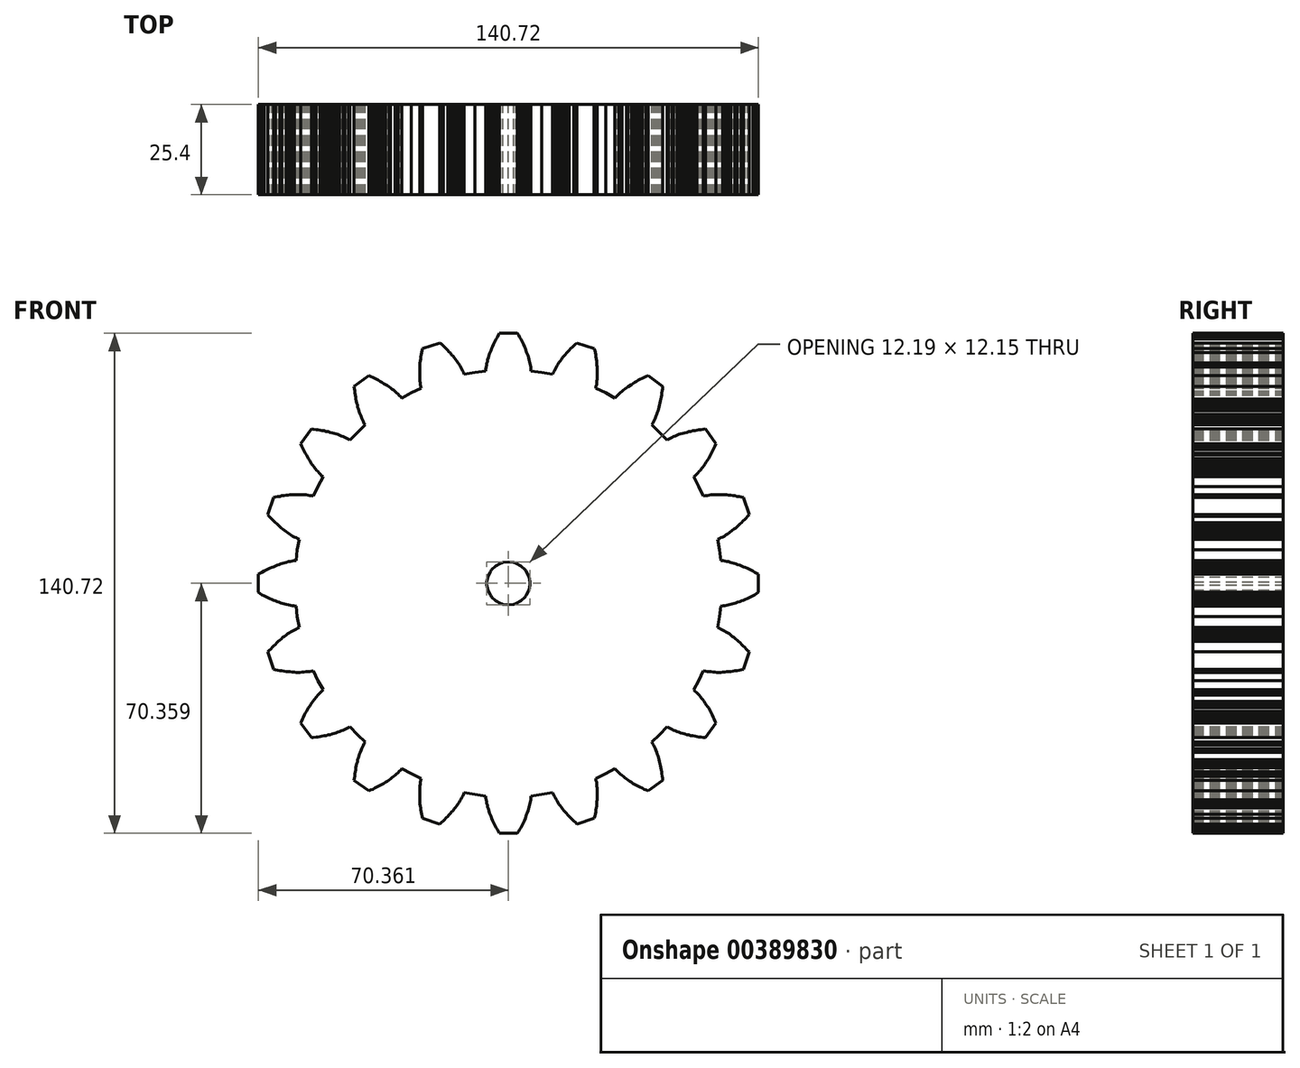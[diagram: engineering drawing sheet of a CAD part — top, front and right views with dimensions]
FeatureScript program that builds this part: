
annotation { "Feature Type Name" : "Feature", "Feature Type Description" : "" }
export const myFeature = defineFeature(function(context is Context, id is Id, definition is map)
    precondition{}
    {
        {
            var Q0;
            Q0=qCreatedBy(makeId("Front.planeOp"),FACE);
            var sketch = newSketch(context, id + "F0", { "sketchPlane" : qUnion([Q0])});
            skLineSegment(sketch, "E0", {"start": v(-98.04, 127.68) * mm, "end": v(-97.87, 127.68) * mm});
            skLineSegment(sketch, "E1", {"start": v(5.93, 25.9) * mm, "end": v(5.93, 25.45) * mm});
            skLineSegment(sketch, "E2", {"start": v(5.93, 25.45) * mm, "end": v(5.62, 24.07) * mm});
            skLineSegment(sketch, "E3", {"start": v(5.62, 24.07) * mm, "end": v(4.93, 22.63) * mm});
            skLineSegment(sketch, "E4", {"start": v(4.93, 22.63) * mm, "end": v(4.74, 22.35) * mm});
            skLineSegment(sketch, "E5", {"start": v(4.74, 22.35) * mm, "end": v(4.55, 22.08) * mm});
            skLineSegment(sketch, "E6", {"start": v(4.55, 22.08) * mm, "end": v(3.4, 21) * mm});
            skLineSegment(sketch, "E7", {"start": v(3.4, 21) * mm, "end": v(2, 20.26) * mm});
            skLineSegment(sketch, "E8", {"start": v(2, 20.26) * mm, "end": v(1.7, 20.15) * mm});
            skLineSegment(sketch, "E9", {"start": v(1.7, 20.15) * mm, "end": v(1.37, 20.05) * mm});
            skLineSegment(sketch, "E10", {"start": v(1.37, 20.05) * mm, "end": v(-0.17, 19.83) * mm});
            skLineSegment(sketch, "E11", {"start": v(-0.17, 19.83) * mm, "end": v(-1.72, 20.05) * mm});
            skLineSegment(sketch, "E12", {"start": v(-1.72, 20.05) * mm, "end": v(-2.03, 20.15) * mm});
            skLineSegment(sketch, "E13", {"start": v(-2.03, 20.15) * mm, "end": v(-2.35, 20.26) * mm});
            skLineSegment(sketch, "E14", {"start": v(-2.35, 20.26) * mm, "end": v(-3.75, 21) * mm});
            skLineSegment(sketch, "E15", {"start": v(-3.75, 21) * mm, "end": v(-4.9, 22.08) * mm});
            skLineSegment(sketch, "E16", {"start": v(-4.9, 22.08) * mm, "end": v(-5.08, 22.35) * mm});
            skLineSegment(sketch, "E17", {"start": v(-5.08, 22.35) * mm, "end": v(-5.27, 22.63) * mm});
            skLineSegment(sketch, "E18", {"start": v(-5.27, 22.63) * mm, "end": v(-5.96, 24.07) * mm});
            skLineSegment(sketch, "E19", {"start": v(-5.96, 24.07) * mm, "end": v(-6.27, 25.45) * mm});
            skLineSegment(sketch, "E20", {"start": v(-6.27, 25.45) * mm, "end": v(-6.27, 25.9) * mm});
            skLineSegment(sketch, "E21", {"start": v(-6.27, 25.9) * mm, "end": v(-6.27, 26.37) * mm});
            skLineSegment(sketch, "E22", {"start": v(-6.27, 26.37) * mm, "end": v(-5.96, 27.75) * mm});
            skLineSegment(sketch, "E23", {"start": v(-5.96, 27.75) * mm, "end": v(-5.27, 29.2) * mm});
            skLineSegment(sketch, "E24", {"start": v(-5.27, 29.2) * mm, "end": v(-5.08, 29.46) * mm});
            skLineSegment(sketch, "E25", {"start": v(-5.08, 29.46) * mm, "end": v(-4.9, 29.74) * mm});
            skLineSegment(sketch, "E26", {"start": v(-4.9, 29.74) * mm, "end": v(-3.75, 30.82) * mm});
            skLineSegment(sketch, "E27", {"start": v(-3.75, 30.82) * mm, "end": v(-2.35, 31.56) * mm});
            skLineSegment(sketch, "E28", {"start": v(-2.35, 31.56) * mm, "end": v(-2.03, 31.67) * mm});
            skLineSegment(sketch, "E29", {"start": v(-2.03, 31.67) * mm, "end": v(-1.72, 31.77) * mm});
            skLineSegment(sketch, "E30", {"start": v(-1.72, 31.77) * mm, "end": v(-0.17, 31.98) * mm});
            skLineSegment(sketch, "E31", {"start": v(-0.17, 31.98) * mm, "end": v(1.37, 31.77) * mm});
            skLineSegment(sketch, "E32", {"start": v(1.37, 31.77) * mm, "end": v(1.7, 31.67) * mm});
            skLineSegment(sketch, "E33", {"start": v(1.7, 31.67) * mm, "end": v(2, 31.56) * mm});
            skLineSegment(sketch, "E34", {"start": v(2, 31.56) * mm, "end": v(3.4, 30.82) * mm});
            skLineSegment(sketch, "E35", {"start": v(3.4, 30.82) * mm, "end": v(4.55, 29.74) * mm});
            skLineSegment(sketch, "E36", {"start": v(4.55, 29.74) * mm, "end": v(4.74, 29.46) * mm});
            skLineSegment(sketch, "E37", {"start": v(4.74, 29.46) * mm, "end": v(4.93, 29.2) * mm});
            skLineSegment(sketch, "E38", {"start": v(4.93, 29.2) * mm, "end": v(5.62, 27.75) * mm});
            skLineSegment(sketch, "E39", {"start": v(5.62, 27.75) * mm, "end": v(5.93, 26.37) * mm});
            skLineSegment(sketch, "E40", {"start": v(5.93, 26.37) * mm, "end": v(5.93, 25.9) * mm});
            skLineSegment(sketch, "E41", {"start": v(59.27, 16.5) * mm, "end": v(59.6, 19.47) * mm});
            skLineSegment(sketch, "E42", {"start": v(59.6, 19.47) * mm, "end": v(60.2, 19.56) * mm});
            skLineSegment(sketch, "E43", {"start": v(60.2, 19.56) * mm, "end": v(60.7, 19.64) * mm});
            skLineSegment(sketch, "E44", {"start": v(60.7, 19.64) * mm, "end": v(61.21, 19.73) * mm});
            skLineSegment(sketch, "E45", {"start": v(61.21, 19.73) * mm, "end": v(61.72, 19.81) * mm});
            skLineSegment(sketch, "E46", {"start": v(61.72, 19.81) * mm, "end": v(62.23, 19.98) * mm});
            skLineSegment(sketch, "E47", {"start": v(62.23, 19.98) * mm, "end": v(62.82, 20.07) * mm});
            skLineSegment(sketch, "E48", {"start": v(62.82, 20.07) * mm, "end": v(63.33, 20.24) * mm});
            skLineSegment(sketch, "E49", {"start": v(63.33, 20.24) * mm, "end": v(63.84, 20.4) * mm});
            skLineSegment(sketch, "E50", {"start": v(63.84, 20.4) * mm, "end": v(64.35, 20.57) * mm});
            skLineSegment(sketch, "E51", {"start": v(64.35, 20.57) * mm, "end": v(64.94, 20.74) * mm});
            skLineSegment(sketch, "E52", {"start": v(64.94, 20.74) * mm, "end": v(65.45, 21) * mm});
            skLineSegment(sketch, "E53", {"start": v(65.45, 21) * mm, "end": v(65.95, 21.17) * mm});
            skLineSegment(sketch, "E54", {"start": v(65.95, 21.17) * mm, "end": v(66.46, 21.42) * mm});
            skLineSegment(sketch, "E55", {"start": v(66.46, 21.42) * mm, "end": v(67.06, 21.67) * mm});
            skLineSegment(sketch, "E56", {"start": v(67.06, 21.67) * mm, "end": v(67.56, 21.93) * mm});
            skLineSegment(sketch, "E57", {"start": v(67.56, 21.93) * mm, "end": v(68.07, 22.18) * mm});
            skLineSegment(sketch, "E58", {"start": v(68.07, 22.18) * mm, "end": v(68.58, 22.44) * mm});
            skLineSegment(sketch, "E59", {"start": v(68.58, 22.44) * mm, "end": v(69.17, 22.7) * mm});
            skLineSegment(sketch, "E60", {"start": v(69.17, 22.7) * mm, "end": v(69.68, 23.03) * mm});
            skLineSegment(sketch, "E61", {"start": v(69.68, 23.03) * mm, "end": v(70.19, 23.37) * mm});
            skLineSegment(sketch, "E62", {"start": v(70.19, 23.37) * mm, "end": v(70.19, 28.45) * mm});
            skLineSegment(sketch, "E63", {"start": v(70.19, 28.45) * mm, "end": v(69.68, 28.79) * mm});
            skLineSegment(sketch, "E64", {"start": v(69.68, 28.79) * mm, "end": v(69.17, 29.04) * mm});
            skLineSegment(sketch, "E65", {"start": v(69.17, 29.04) * mm, "end": v(68.58, 29.38) * mm});
            skLineSegment(sketch, "E66", {"start": v(68.58, 29.38) * mm, "end": v(68.07, 29.63) * mm});
            skLineSegment(sketch, "E67", {"start": v(68.07, 29.63) * mm, "end": v(67.56, 29.89) * mm});
            skLineSegment(sketch, "E68", {"start": v(67.56, 29.89) * mm, "end": v(67.06, 30.14) * mm});
            skLineSegment(sketch, "E69", {"start": v(67.06, 30.14) * mm, "end": v(66.46, 30.4) * mm});
            skLineSegment(sketch, "E70", {"start": v(66.46, 30.4) * mm, "end": v(65.95, 30.56) * mm});
            skLineSegment(sketch, "E71", {"start": v(65.95, 30.56) * mm, "end": v(65.45, 30.82) * mm});
            skLineSegment(sketch, "E72", {"start": v(65.45, 30.82) * mm, "end": v(64.94, 30.99) * mm});
            skLineSegment(sketch, "E73", {"start": v(64.94, 30.99) * mm, "end": v(64.35, 31.16) * mm});
            skLineSegment(sketch, "E74", {"start": v(64.35, 31.16) * mm, "end": v(63.84, 31.41) * mm});
            skLineSegment(sketch, "E75", {"start": v(63.84, 31.41) * mm, "end": v(63.33, 31.58) * mm});
            skLineSegment(sketch, "E76", {"start": v(63.33, 31.58) * mm, "end": v(62.82, 31.67) * mm});
            skLineSegment(sketch, "E77", {"start": v(62.82, 31.67) * mm, "end": v(62.23, 31.83) * mm});
            skLineSegment(sketch, "E78", {"start": v(62.23, 31.83) * mm, "end": v(61.72, 32) * mm});
            skLineSegment(sketch, "E79", {"start": v(61.72, 32) * mm, "end": v(61.21, 32.09) * mm});
            skLineSegment(sketch, "E80", {"start": v(61.21, 32.09) * mm, "end": v(60.7, 32.17) * mm});
            skLineSegment(sketch, "E81", {"start": v(60.7, 32.17) * mm, "end": v(60.2, 32.26) * mm});
            skLineSegment(sketch, "E82", {"start": v(60.2, 32.26) * mm, "end": v(59.6, 32.26) * mm});
            skLineSegment(sketch, "E83", {"start": v(59.6, 32.26) * mm, "end": v(59.27, 35.3) * mm});
            skLineSegment(sketch, "E84", {"start": v(59.27, 35.3) * mm, "end": v(58.67, 38.27) * mm});
            skLineSegment(sketch, "E85", {"start": v(58.67, 38.27) * mm, "end": v(59.18, 38.52) * mm});
            skLineSegment(sketch, "E86", {"start": v(59.18, 38.52) * mm, "end": v(59.6, 38.78) * mm});
            skLineSegment(sketch, "E87", {"start": v(59.6, 38.78) * mm, "end": v(60.11, 38.95) * mm});
            skLineSegment(sketch, "E88", {"start": v(60.11, 38.95) * mm, "end": v(60.62, 39.2) * mm});
            skLineSegment(sketch, "E89", {"start": v(60.62, 39.2) * mm, "end": v(61.05, 39.54) * mm});
            skLineSegment(sketch, "E90", {"start": v(61.05, 39.54) * mm, "end": v(61.47, 39.8) * mm});
            skLineSegment(sketch, "E91", {"start": v(61.47, 39.8) * mm, "end": v(61.98, 40.13) * mm});
            skLineSegment(sketch, "E92", {"start": v(61.98, 40.13) * mm, "end": v(62.4, 40.47) * mm});
            skLineSegment(sketch, "E93", {"start": v(62.4, 40.47) * mm, "end": v(62.82, 40.81) * mm});
            skLineSegment(sketch, "E94", {"start": v(62.82, 40.81) * mm, "end": v(63.33, 41.15) * mm});
            skLineSegment(sketch, "E95", {"start": v(63.33, 41.15) * mm, "end": v(63.75, 41.49) * mm});
            skLineSegment(sketch, "E96", {"start": v(63.75, 41.49) * mm, "end": v(64.18, 41.83) * mm});
            skLineSegment(sketch, "E97", {"start": v(64.18, 41.83) * mm, "end": v(64.6, 42.25) * mm});
            skLineSegment(sketch, "E98", {"start": v(64.6, 42.25) * mm, "end": v(65.02, 42.67) * mm});
            skLineSegment(sketch, "E99", {"start": v(65.02, 42.67) * mm, "end": v(65.45, 43.01) * mm});
            skLineSegment(sketch, "E100", {"start": v(65.45, 43.01) * mm, "end": v(65.87, 43.43) * mm});
            skLineSegment(sketch, "E101", {"start": v(65.87, 43.43) * mm, "end": v(66.3, 43.86) * mm});
            skLineSegment(sketch, "E102", {"start": v(66.3, 43.86) * mm, "end": v(66.72, 44.28) * mm});
            skLineSegment(sketch, "E103", {"start": v(66.72, 44.28) * mm, "end": v(67.14, 44.7) * mm});
            skLineSegment(sketch, "E104", {"start": v(67.14, 44.7) * mm, "end": v(67.56, 45.21) * mm});
            skLineSegment(sketch, "E105", {"start": v(67.56, 45.21) * mm, "end": v(65.95, 50.04) * mm});
            skLineSegment(sketch, "E106", {"start": v(65.95, 50.04) * mm, "end": v(65.36, 50.2) * mm});
            skLineSegment(sketch, "E107", {"start": v(65.36, 50.2) * mm, "end": v(64.77, 50.3) * mm});
            skLineSegment(sketch, "E108", {"start": v(64.77, 50.3) * mm, "end": v(64.18, 50.38) * mm});
            skLineSegment(sketch, "E109", {"start": v(64.18, 50.38) * mm, "end": v(63.58, 50.55) * mm});
            skLineSegment(sketch, "E110", {"start": v(63.58, 50.55) * mm, "end": v(63, 50.63) * mm});
            skLineSegment(sketch, "E111", {"start": v(63, 50.63) * mm, "end": v(62.4, 50.72) * mm});
            skLineSegment(sketch, "E112", {"start": v(62.4, 50.72) * mm, "end": v(61.8, 50.72) * mm});
            skLineSegment(sketch, "E113", {"start": v(61.8, 50.72) * mm, "end": v(61.3, 50.8) * mm});
            skLineSegment(sketch, "E114", {"start": v(61.3, 50.8) * mm, "end": v(60.7, 50.8) * mm});
            skLineSegment(sketch, "E115", {"start": v(60.7, 50.8) * mm, "end": v(60.11, 50.88) * mm});
            skLineSegment(sketch, "E116", {"start": v(60.11, 50.88) * mm, "end": v(59.6, 50.88) * mm});
            skLineSegment(sketch, "E117", {"start": v(59.6, 50.88) * mm, "end": v(59.01, 50.88) * mm});
            skLineSegment(sketch, "E118", {"start": v(59.01, 50.88) * mm, "end": v(58.5, 50.88) * mm});
            skLineSegment(sketch, "E119", {"start": v(58.5, 50.88) * mm, "end": v(57.91, 50.88) * mm});
            skLineSegment(sketch, "E120", {"start": v(57.91, 50.88) * mm, "end": v(57.4, 50.8) * mm});
            skLineSegment(sketch, "E121", {"start": v(57.4, 50.8) * mm, "end": v(56.81, 50.8) * mm});
            skLineSegment(sketch, "E122", {"start": v(56.81, 50.8) * mm, "end": v(56.3, 50.72) * mm});
            skLineSegment(sketch, "E123", {"start": v(56.3, 50.72) * mm, "end": v(55.8, 50.63) * mm});
            skLineSegment(sketch, "E124", {"start": v(55.8, 50.63) * mm, "end": v(55.29, 50.55) * mm});
            skLineSegment(sketch, "E125", {"start": v(55.29, 50.55) * mm, "end": v(54.7, 50.46) * mm});
            skLineSegment(sketch, "E126", {"start": v(54.7, 50.46) * mm, "end": v(53.42, 53.17) * mm});
            skLineSegment(sketch, "E127", {"start": v(53.42, 53.17) * mm, "end": v(51.99, 55.88) * mm});
            skLineSegment(sketch, "E128", {"start": v(51.99, 55.88) * mm, "end": v(52.32, 56.22) * mm});
            skLineSegment(sketch, "E129", {"start": v(52.32, 56.22) * mm, "end": v(52.75, 56.56) * mm});
            skLineSegment(sketch, "E130", {"start": v(52.75, 56.56) * mm, "end": v(53.09, 56.98) * mm});
            skLineSegment(sketch, "E131", {"start": v(53.09, 56.98) * mm, "end": v(53.5, 57.4) * mm});
            skLineSegment(sketch, "E132", {"start": v(53.5, 57.4) * mm, "end": v(53.85, 57.74) * mm});
            skLineSegment(sketch, "E133", {"start": v(53.85, 57.74) * mm, "end": v(54.19, 58.17) * mm});
            skLineSegment(sketch, "E134", {"start": v(54.19, 58.17) * mm, "end": v(54.53, 58.59) * mm});
            skLineSegment(sketch, "E135", {"start": v(54.53, 58.59) * mm, "end": v(54.86, 59.1) * mm});
            skLineSegment(sketch, "E136", {"start": v(54.86, 59.1) * mm, "end": v(55.2, 59.52) * mm});
            skLineSegment(sketch, "E137", {"start": v(55.2, 59.52) * mm, "end": v(55.46, 60.03) * mm});
            skLineSegment(sketch, "E138", {"start": v(55.46, 60.03) * mm, "end": v(55.8, 60.45) * mm});
            skLineSegment(sketch, "E139", {"start": v(55.8, 60.45) * mm, "end": v(56.13, 60.96) * mm});
            skLineSegment(sketch, "E140", {"start": v(56.13, 60.96) * mm, "end": v(56.39, 61.47) * mm});
            skLineSegment(sketch, "E141", {"start": v(56.39, 61.47) * mm, "end": v(56.64, 61.98) * mm});
            skLineSegment(sketch, "E142", {"start": v(56.64, 61.98) * mm, "end": v(56.98, 62.48) * mm});
            skLineSegment(sketch, "E143", {"start": v(56.98, 62.48) * mm, "end": v(57.23, 63) * mm});
            skLineSegment(sketch, "E144", {"start": v(57.23, 63) * mm, "end": v(57.49, 63.5) * mm});
            skLineSegment(sketch, "E145", {"start": v(57.49, 63.5) * mm, "end": v(57.74, 64.1) * mm});
            skLineSegment(sketch, "E146", {"start": v(57.74, 64.1) * mm, "end": v(58, 64.6) * mm});
            skLineSegment(sketch, "E147", {"start": v(58, 64.6) * mm, "end": v(58.25, 65.2) * mm});
            skLineSegment(sketch, "E148", {"start": v(58.25, 65.2) * mm, "end": v(55.29, 69.34) * mm});
            skLineSegment(sketch, "E149", {"start": v(55.29, 69.34) * mm, "end": v(54.6, 69.26) * mm});
            skLineSegment(sketch, "E150", {"start": v(54.6, 69.26) * mm, "end": v(54.02, 69.17) * mm});
            skLineSegment(sketch, "E151", {"start": v(54.02, 69.17) * mm, "end": v(53.42, 69.09) * mm});
            skLineSegment(sketch, "E152", {"start": v(53.42, 69.09) * mm, "end": v(52.83, 69) * mm});
            skLineSegment(sketch, "E153", {"start": v(52.83, 69) * mm, "end": v(52.32, 68.92) * mm});
            skLineSegment(sketch, "E154", {"start": v(52.32, 68.92) * mm, "end": v(51.73, 68.83) * mm});
            skLineSegment(sketch, "E155", {"start": v(51.73, 68.83) * mm, "end": v(51.14, 68.66) * mm});
            skLineSegment(sketch, "E156", {"start": v(51.14, 68.66) * mm, "end": v(50.55, 68.58) * mm});
            skLineSegment(sketch, "E157", {"start": v(50.55, 68.58) * mm, "end": v(50.04, 68.41) * mm});
            skLineSegment(sketch, "E158", {"start": v(50.04, 68.41) * mm, "end": v(49.44, 68.24) * mm});
            skLineSegment(sketch, "E159", {"start": v(49.44, 68.24) * mm, "end": v(48.94, 68.16) * mm});
            skLineSegment(sketch, "E160", {"start": v(48.94, 68.16) * mm, "end": v(48.35, 67.99) * mm});
            skLineSegment(sketch, "E161", {"start": v(48.35, 67.99) * mm, "end": v(47.84, 67.82) * mm});
            skLineSegment(sketch, "E162", {"start": v(47.84, 67.82) * mm, "end": v(47.33, 67.56) * mm});
            skLineSegment(sketch, "E163", {"start": v(47.33, 67.56) * mm, "end": v(46.82, 67.4) * mm});
            skLineSegment(sketch, "E164", {"start": v(46.82, 67.4) * mm, "end": v(46.31, 67.23) * mm});
            skLineSegment(sketch, "E165", {"start": v(46.31, 67.23) * mm, "end": v(45.89, 66.97) * mm});
            skLineSegment(sketch, "E166", {"start": v(45.89, 66.97) * mm, "end": v(45.38, 66.72) * mm});
            skLineSegment(sketch, "E167", {"start": v(45.38, 66.72) * mm, "end": v(44.87, 66.46) * mm});
            skLineSegment(sketch, "E168", {"start": v(44.87, 66.46) * mm, "end": v(44.45, 66.21) * mm});
            skLineSegment(sketch, "E169", {"start": v(44.45, 66.21) * mm, "end": v(42.33, 68.41) * mm});
            skLineSegment(sketch, "E170", {"start": v(42.33, 68.41) * mm, "end": v(40.13, 70.53) * mm});
            skLineSegment(sketch, "E171", {"start": v(40.13, 70.53) * mm, "end": v(40.39, 70.95) * mm});
            skLineSegment(sketch, "E172", {"start": v(40.39, 70.95) * mm, "end": v(40.64, 71.46) * mm});
            skLineSegment(sketch, "E173", {"start": v(40.64, 71.46) * mm, "end": v(40.9, 71.88) * mm});
            skLineSegment(sketch, "E174", {"start": v(40.9, 71.88) * mm, "end": v(41.15, 72.4) * mm});
            skLineSegment(sketch, "E175", {"start": v(41.15, 72.4) * mm, "end": v(41.32, 72.9) * mm});
            skLineSegment(sketch, "E176", {"start": v(41.32, 72.9) * mm, "end": v(41.57, 73.4) * mm});
            skLineSegment(sketch, "E177", {"start": v(41.57, 73.4) * mm, "end": v(41.74, 73.91) * mm});
            skLineSegment(sketch, "E178", {"start": v(41.74, 73.91) * mm, "end": v(41.9, 74.42) * mm});
            skLineSegment(sketch, "E179", {"start": v(41.9, 74.42) * mm, "end": v(42.08, 75.01) * mm});
            skLineSegment(sketch, "E180", {"start": v(42.08, 75.01) * mm, "end": v(42.25, 75.52) * mm});
            skLineSegment(sketch, "E181", {"start": v(42.25, 75.52) * mm, "end": v(42.33, 76.12) * mm});
            skLineSegment(sketch, "E182", {"start": v(42.33, 76.12) * mm, "end": v(42.5, 76.62) * mm});
            skLineSegment(sketch, "E183", {"start": v(42.5, 76.62) * mm, "end": v(42.59, 77.22) * mm});
            skLineSegment(sketch, "E184", {"start": v(42.59, 77.22) * mm, "end": v(42.76, 77.72) * mm});
            skLineSegment(sketch, "E185", {"start": v(42.76, 77.72) * mm, "end": v(42.84, 78.32) * mm});
            skLineSegment(sketch, "E186", {"start": v(42.84, 78.32) * mm, "end": v(42.93, 78.91) * mm});
            skLineSegment(sketch, "E187", {"start": v(42.93, 78.91) * mm, "end": v(43.01, 79.5) * mm});
            skLineSegment(sketch, "E188", {"start": v(43.01, 79.5) * mm, "end": v(43.1, 80.1) * mm});
            skLineSegment(sketch, "E189", {"start": v(43.1, 80.1) * mm, "end": v(43.18, 80.69) * mm});
            skLineSegment(sketch, "E190", {"start": v(43.18, 80.69) * mm, "end": v(43.26, 81.28) * mm});
            skLineSegment(sketch, "E191", {"start": v(43.26, 81.28) * mm, "end": v(39.12, 84.33) * mm});
            skLineSegment(sketch, "E192", {"start": v(39.12, 84.33) * mm, "end": v(38.52, 84.07) * mm});
            skLineSegment(sketch, "E193", {"start": v(38.52, 84.07) * mm, "end": v(38.02, 83.82) * mm});
            skLineSegment(sketch, "E194", {"start": v(38.02, 83.82) * mm, "end": v(37.5, 83.57) * mm});
            skLineSegment(sketch, "E195", {"start": v(37.5, 83.57) * mm, "end": v(36.91, 83.31) * mm});
            skLineSegment(sketch, "E196", {"start": v(36.91, 83.31) * mm, "end": v(36.4, 83.06) * mm});
            skLineSegment(sketch, "E197", {"start": v(36.4, 83.06) * mm, "end": v(35.9, 82.72) * mm});
            skLineSegment(sketch, "E198", {"start": v(35.9, 82.72) * mm, "end": v(35.39, 82.47) * mm});
            skLineSegment(sketch, "E199", {"start": v(35.39, 82.47) * mm, "end": v(34.88, 82.13) * mm});
            skLineSegment(sketch, "E200", {"start": v(34.88, 82.13) * mm, "end": v(34.46, 81.87) * mm});
            skLineSegment(sketch, "E201", {"start": v(34.46, 81.87) * mm, "end": v(33.95, 81.53) * mm});
            skLineSegment(sketch, "E202", {"start": v(33.95, 81.53) * mm, "end": v(33.44, 81.2) * mm});
            skLineSegment(sketch, "E203", {"start": v(33.44, 81.2) * mm, "end": v(33.02, 80.94) * mm});
            skLineSegment(sketch, "E204", {"start": v(33.02, 80.94) * mm, "end": v(32.6, 80.6) * mm});
            skLineSegment(sketch, "E205", {"start": v(32.6, 80.6) * mm, "end": v(32.17, 80.26) * mm});
            skLineSegment(sketch, "E206", {"start": v(32.17, 80.26) * mm, "end": v(31.75, 79.93) * mm});
            skLineSegment(sketch, "E207", {"start": v(31.75, 79.93) * mm, "end": v(31.33, 79.5) * mm});
            skLineSegment(sketch, "E208", {"start": v(31.33, 79.5) * mm, "end": v(30.9, 79.16) * mm});
            skLineSegment(sketch, "E209", {"start": v(30.9, 79.16) * mm, "end": v(30.56, 78.82) * mm});
            skLineSegment(sketch, "E210", {"start": v(30.56, 78.82) * mm, "end": v(30.14, 78.4) * mm});
            skLineSegment(sketch, "E211", {"start": v(30.14, 78.4) * mm, "end": v(29.8, 78.06) * mm});
            skLineSegment(sketch, "E212", {"start": v(29.8, 78.06) * mm, "end": v(27.18, 79.5) * mm});
            skLineSegment(sketch, "E213", {"start": v(27.18, 79.5) * mm, "end": v(24.38, 80.77) * mm});
            skLineSegment(sketch, "E214", {"start": v(24.38, 80.77) * mm, "end": v(24.47, 81.28) * mm});
            skLineSegment(sketch, "E215", {"start": v(24.47, 81.28) * mm, "end": v(24.64, 81.87) * mm});
            skLineSegment(sketch, "E216", {"start": v(24.64, 81.87) * mm, "end": v(24.64, 82.38) * mm});
            skLineSegment(sketch, "E217", {"start": v(24.64, 82.38) * mm, "end": v(24.72, 82.89) * mm});
            skLineSegment(sketch, "E218", {"start": v(24.72, 82.89) * mm, "end": v(24.8, 83.4) * mm});
            skLineSegment(sketch, "E219", {"start": v(24.8, 83.4) * mm, "end": v(24.8, 83.99) * mm});
            skLineSegment(sketch, "E220", {"start": v(24.8, 83.99) * mm, "end": v(24.8, 84.5) * mm});
            skLineSegment(sketch, "E221", {"start": v(24.8, 84.5) * mm, "end": v(24.8, 85.1) * mm});
            skLineSegment(sketch, "E222", {"start": v(24.8, 85.1) * mm, "end": v(24.8, 85.6) * mm});
            skLineSegment(sketch, "E223", {"start": v(24.8, 85.6) * mm, "end": v(24.8, 86.2) * mm});
            skLineSegment(sketch, "E224", {"start": v(24.8, 86.2) * mm, "end": v(24.8, 86.78) * mm});
            skLineSegment(sketch, "E225", {"start": v(24.8, 86.78) * mm, "end": v(24.72, 87.38) * mm});
            skLineSegment(sketch, "E226", {"start": v(24.72, 87.38) * mm, "end": v(24.72, 87.88) * mm});
            skLineSegment(sketch, "E227", {"start": v(24.72, 87.88) * mm, "end": v(24.64, 88.48) * mm});
            skLineSegment(sketch, "E228", {"start": v(24.64, 88.48) * mm, "end": v(24.55, 89.07) * mm});
            skLineSegment(sketch, "E229", {"start": v(24.55, 89.07) * mm, "end": v(24.47, 89.66) * mm});
            skLineSegment(sketch, "E230", {"start": v(24.47, 89.66) * mm, "end": v(24.38, 90.26) * mm});
            skLineSegment(sketch, "E231", {"start": v(24.38, 90.26) * mm, "end": v(24.3, 90.85) * mm});
            skLineSegment(sketch, "E232", {"start": v(24.3, 90.85) * mm, "end": v(24.13, 91.44) * mm});
            skLineSegment(sketch, "E233", {"start": v(24.13, 91.44) * mm, "end": v(23.96, 92.03) * mm});
            skLineSegment(sketch, "E234", {"start": v(23.96, 92.03) * mm, "end": v(19.13, 93.56) * mm});
            skLineSegment(sketch, "E235", {"start": v(19.13, 93.56) * mm, "end": v(18.71, 93.22) * mm});
            skLineSegment(sketch, "E236", {"start": v(18.71, 93.22) * mm, "end": v(18.2, 92.8) * mm});
            skLineSegment(sketch, "E237", {"start": v(18.2, 92.8) * mm, "end": v(17.78, 92.37) * mm});
            skLineSegment(sketch, "E238", {"start": v(17.78, 92.37) * mm, "end": v(17.36, 91.95) * mm});
            skLineSegment(sketch, "E239", {"start": v(17.36, 91.95) * mm, "end": v(16.93, 91.52) * mm});
            skLineSegment(sketch, "E240", {"start": v(16.93, 91.52) * mm, "end": v(16.6, 91.1) * mm});
            skLineSegment(sketch, "E241", {"start": v(16.6, 91.1) * mm, "end": v(16.17, 90.68) * mm});
            skLineSegment(sketch, "E242", {"start": v(16.17, 90.68) * mm, "end": v(15.83, 90.26) * mm});
            skLineSegment(sketch, "E243", {"start": v(15.83, 90.26) * mm, "end": v(15.4, 89.83) * mm});
            skLineSegment(sketch, "E244", {"start": v(15.4, 89.83) * mm, "end": v(15.07, 89.4) * mm});
            skLineSegment(sketch, "E245", {"start": v(15.07, 89.4) * mm, "end": v(14.73, 88.9) * mm});
            skLineSegment(sketch, "E246", {"start": v(14.73, 88.9) * mm, "end": v(14.4, 88.48) * mm});
            skLineSegment(sketch, "E247", {"start": v(14.4, 88.48) * mm, "end": v(14.06, 88.05) * mm});
            skLineSegment(sketch, "E248", {"start": v(14.06, 88.05) * mm, "end": v(13.72, 87.54) * mm});
            skLineSegment(sketch, "E249", {"start": v(13.72, 87.54) * mm, "end": v(13.46, 87.12) * mm});
            skLineSegment(sketch, "E250", {"start": v(13.46, 87.12) * mm, "end": v(13.2, 86.61) * mm});
            skLineSegment(sketch, "E251", {"start": v(13.2, 86.61) * mm, "end": v(12.95, 86.2) * mm});
            skLineSegment(sketch, "E252", {"start": v(12.95, 86.2) * mm, "end": v(12.7, 85.68) * mm});
            skLineSegment(sketch, "E253", {"start": v(12.7, 85.68) * mm, "end": v(12.45, 85.26) * mm});
            skLineSegment(sketch, "E254", {"start": v(12.45, 85.26) * mm, "end": v(12.28, 84.75) * mm});
            skLineSegment(sketch, "E255", {"start": v(12.28, 84.75) * mm, "end": v(9.23, 85.26) * mm});
            skLineSegment(sketch, "E256", {"start": v(9.23, 85.26) * mm, "end": v(6.18, 85.68) * mm});
            skLineSegment(sketch, "E257", {"start": v(6.18, 85.68) * mm, "end": v(6.18, 86.2) * mm});
            skLineSegment(sketch, "E258", {"start": v(6.18, 86.2) * mm, "end": v(6.1, 86.78) * mm});
            skLineSegment(sketch, "E259", {"start": v(6.1, 86.78) * mm, "end": v(6.01, 87.3) * mm});
            skLineSegment(sketch, "E260", {"start": v(6.01, 87.3) * mm, "end": v(5.93, 87.8) * mm});
            skLineSegment(sketch, "E261", {"start": v(5.93, 87.8) * mm, "end": v(5.76, 88.3) * mm});
            skLineSegment(sketch, "E262", {"start": v(5.76, 88.3) * mm, "end": v(5.67, 88.82) * mm});
            skLineSegment(sketch, "E263", {"start": v(5.67, 88.82) * mm, "end": v(5.5, 89.4) * mm});
            skLineSegment(sketch, "E264", {"start": v(5.5, 89.4) * mm, "end": v(5.33, 89.92) * mm});
            skLineSegment(sketch, "E265", {"start": v(5.33, 89.92) * mm, "end": v(5.16, 90.42) * mm});
            skLineSegment(sketch, "E266", {"start": v(5.16, 90.42) * mm, "end": v(4.91, 90.93) * mm});
            skLineSegment(sketch, "E267", {"start": v(4.91, 90.93) * mm, "end": v(4.74, 91.52) * mm});
            skLineSegment(sketch, "E268", {"start": v(4.74, 91.52) * mm, "end": v(4.57, 92.03) * mm});
            skLineSegment(sketch, "E269", {"start": v(4.57, 92.03) * mm, "end": v(4.32, 92.54) * mm});
            skLineSegment(sketch, "E270", {"start": v(4.32, 92.54) * mm, "end": v(4.06, 93.13) * mm});
            skLineSegment(sketch, "E271", {"start": v(4.06, 93.13) * mm, "end": v(3.8, 93.64) * mm});
            skLineSegment(sketch, "E272", {"start": v(3.8, 93.64) * mm, "end": v(3.56, 94.15) * mm});
            skLineSegment(sketch, "E273", {"start": v(3.56, 94.15) * mm, "end": v(3.3, 94.66) * mm});
            skLineSegment(sketch, "E274", {"start": v(3.3, 94.66) * mm, "end": v(2.96, 95.17) * mm});
            skLineSegment(sketch, "E275", {"start": v(2.96, 95.17) * mm, "end": v(2.7, 95.76) * mm});
            skLineSegment(sketch, "E276", {"start": v(2.7, 95.76) * mm, "end": v(2.37, 96.27) * mm});
            skLineSegment(sketch, "E277", {"start": v(2.37, 96.27) * mm, "end": v(-2.71, 96.27) * mm});
            skLineSegment(sketch, "E278", {"start": v(-2.71, 96.27) * mm, "end": v(-3.05, 95.76) * mm});
            skLineSegment(sketch, "E279", {"start": v(-3.05, 95.76) * mm, "end": v(-3.3, 95.17) * mm});
            skLineSegment(sketch, "E280", {"start": v(-3.3, 95.17) * mm, "end": v(-3.64, 94.66) * mm});
            skLineSegment(sketch, "E281", {"start": v(-3.64, 94.66) * mm, "end": v(-3.9, 94.15) * mm});
            skLineSegment(sketch, "E282", {"start": v(-3.9, 94.15) * mm, "end": v(-4.15, 93.64) * mm});
            skLineSegment(sketch, "E283", {"start": v(-4.15, 93.64) * mm, "end": v(-4.4, 93.13) * mm});
            skLineSegment(sketch, "E284", {"start": v(-4.4, 93.13) * mm, "end": v(-4.66, 92.54) * mm});
            skLineSegment(sketch, "E285", {"start": v(-4.66, 92.54) * mm, "end": v(-4.91, 92.03) * mm});
            skLineSegment(sketch, "E286", {"start": v(-4.91, 92.03) * mm, "end": v(-5.08, 91.52) * mm});
            skLineSegment(sketch, "E287", {"start": v(-5.08, 91.52) * mm, "end": v(-5.25, 90.93) * mm});
            skLineSegment(sketch, "E288", {"start": v(-5.25, 90.93) * mm, "end": v(-5.5, 90.42) * mm});
            skLineSegment(sketch, "E289", {"start": v(-5.5, 90.42) * mm, "end": v(-5.67, 89.92) * mm});
            skLineSegment(sketch, "E290", {"start": v(-5.67, 89.92) * mm, "end": v(-5.84, 89.4) * mm});
            skLineSegment(sketch, "E291", {"start": v(-5.84, 89.4) * mm, "end": v(-6.01, 88.82) * mm});
            skLineSegment(sketch, "E292", {"start": v(-6.01, 88.82) * mm, "end": v(-6.1, 88.3) * mm});
            skLineSegment(sketch, "E293", {"start": v(-6.1, 88.3) * mm, "end": v(-6.27, 87.8) * mm});
            skLineSegment(sketch, "E294", {"start": v(-6.27, 87.8) * mm, "end": v(-6.35, 87.3) * mm});
            skLineSegment(sketch, "E295", {"start": v(-6.35, 87.3) * mm, "end": v(-6.43, 86.78) * mm});
            skLineSegment(sketch, "E296", {"start": v(-6.43, 86.78) * mm, "end": v(-6.52, 86.2) * mm});
            skLineSegment(sketch, "E297", {"start": v(-6.52, 86.2) * mm, "end": v(-6.52, 85.68) * mm});
            skLineSegment(sketch, "E298", {"start": v(-6.52, 85.68) * mm, "end": v(-9.57, 85.26) * mm});
            skLineSegment(sketch, "E299", {"start": v(-9.57, 85.26) * mm, "end": v(-12.62, 84.75) * mm});
            skLineSegment(sketch, "E300", {"start": v(-12.62, 84.75) * mm, "end": v(-12.78, 85.26) * mm});
            skLineSegment(sketch, "E301", {"start": v(-12.78, 85.26) * mm, "end": v(-13.04, 85.68) * mm});
            skLineSegment(sketch, "E302", {"start": v(-13.04, 85.68) * mm, "end": v(-13.3, 86.2) * mm});
            skLineSegment(sketch, "E303", {"start": v(-13.3, 86.2) * mm, "end": v(-13.55, 86.61) * mm});
            skLineSegment(sketch, "E304", {"start": v(-13.55, 86.61) * mm, "end": v(-13.8, 87.12) * mm});
            skLineSegment(sketch, "E305", {"start": v(-13.8, 87.12) * mm, "end": v(-14.06, 87.54) * mm});
            skLineSegment(sketch, "E306", {"start": v(-14.06, 87.54) * mm, "end": v(-14.4, 88.05) * mm});
            skLineSegment(sketch, "E307", {"start": v(-14.4, 88.05) * mm, "end": v(-14.73, 88.48) * mm});
            skLineSegment(sketch, "E308", {"start": v(-14.73, 88.48) * mm, "end": v(-15.07, 88.9) * mm});
            skLineSegment(sketch, "E309", {"start": v(-15.07, 88.9) * mm, "end": v(-15.41, 89.4) * mm});
            skLineSegment(sketch, "E310", {"start": v(-15.41, 89.4) * mm, "end": v(-15.75, 89.83) * mm});
            skLineSegment(sketch, "E311", {"start": v(-15.75, 89.83) * mm, "end": v(-16.17, 90.26) * mm});
            skLineSegment(sketch, "E312", {"start": v(-16.17, 90.26) * mm, "end": v(-16.5, 90.68) * mm});
            skLineSegment(sketch, "E313", {"start": v(-16.5, 90.68) * mm, "end": v(-16.93, 91.1) * mm});
            skLineSegment(sketch, "E314", {"start": v(-16.93, 91.1) * mm, "end": v(-17.27, 91.52) * mm});
            skLineSegment(sketch, "E315", {"start": v(-17.27, 91.52) * mm, "end": v(-17.7, 91.95) * mm});
            skLineSegment(sketch, "E316", {"start": v(-17.7, 91.95) * mm, "end": v(-18.12, 92.37) * mm});
            skLineSegment(sketch, "E317", {"start": v(-18.12, 92.37) * mm, "end": v(-18.54, 92.8) * mm});
            skLineSegment(sketch, "E318", {"start": v(-18.54, 92.8) * mm, "end": v(-19.05, 93.22) * mm});
            skLineSegment(sketch, "E319", {"start": v(-19.05, 93.22) * mm, "end": v(-19.47, 93.56) * mm});
            skLineSegment(sketch, "E320", {"start": v(-19.47, 93.56) * mm, "end": v(-24.3, 92.03) * mm});
            skLineSegment(sketch, "E321", {"start": v(-24.3, 92.03) * mm, "end": v(-24.47, 91.44) * mm});
            skLineSegment(sketch, "E322", {"start": v(-24.47, 91.44) * mm, "end": v(-24.64, 90.85) * mm});
            skLineSegment(sketch, "E323", {"start": v(-24.64, 90.85) * mm, "end": v(-24.72, 90.26) * mm});
            skLineSegment(sketch, "E324", {"start": v(-24.72, 90.26) * mm, "end": v(-24.8, 89.66) * mm});
            skLineSegment(sketch, "E325", {"start": v(-24.8, 89.66) * mm, "end": v(-24.9, 89.07) * mm});
            skLineSegment(sketch, "E326", {"start": v(-24.9, 89.07) * mm, "end": v(-24.98, 88.48) * mm});
            skLineSegment(sketch, "E327", {"start": v(-24.98, 88.48) * mm, "end": v(-25.06, 87.88) * mm});
            skLineSegment(sketch, "E328", {"start": v(-25.06, 87.88) * mm, "end": v(-25.06, 87.38) * mm});
            skLineSegment(sketch, "E329", {"start": v(-25.06, 87.38) * mm, "end": v(-25.15, 86.78) * mm});
            skLineSegment(sketch, "E330", {"start": v(-25.15, 86.78) * mm, "end": v(-25.15, 86.2) * mm});
            skLineSegment(sketch, "E331", {"start": v(-25.15, 86.2) * mm, "end": v(-25.15, 85.6) * mm});
            skLineSegment(sketch, "E332", {"start": v(-25.15, 85.6) * mm, "end": v(-25.15, 85.1) * mm});
            skLineSegment(sketch, "E333", {"start": v(-25.15, 85.1) * mm, "end": v(-25.15, 84.5) * mm});
            skLineSegment(sketch, "E334", {"start": v(-25.15, 84.5) * mm, "end": v(-25.15, 83.99) * mm});
            skLineSegment(sketch, "E335", {"start": v(-25.15, 83.99) * mm, "end": v(-25.15, 83.4) * mm});
            skLineSegment(sketch, "E336", {"start": v(-25.15, 83.4) * mm, "end": v(-25.06, 82.89) * mm});
            skLineSegment(sketch, "E337", {"start": v(-25.06, 82.89) * mm, "end": v(-24.98, 82.38) * mm});
            skLineSegment(sketch, "E338", {"start": v(-24.98, 82.38) * mm, "end": v(-24.98, 81.87) * mm});
            skLineSegment(sketch, "E339", {"start": v(-24.98, 81.87) * mm, "end": v(-24.8, 81.28) * mm});
            skLineSegment(sketch, "E340", {"start": v(-24.8, 81.28) * mm, "end": v(-24.72, 80.77) * mm});
            skLineSegment(sketch, "E341", {"start": v(-24.72, 80.77) * mm, "end": v(-27.52, 79.5) * mm});
            skLineSegment(sketch, "E342", {"start": v(-27.52, 79.5) * mm, "end": v(-30.14, 78.06) * mm});
            skLineSegment(sketch, "E343", {"start": v(-30.14, 78.06) * mm, "end": v(-30.48, 78.4) * mm});
            skLineSegment(sketch, "E344", {"start": v(-30.48, 78.4) * mm, "end": v(-30.9, 78.82) * mm});
            skLineSegment(sketch, "E345", {"start": v(-30.9, 78.82) * mm, "end": v(-31.24, 79.16) * mm});
            skLineSegment(sketch, "E346", {"start": v(-31.24, 79.16) * mm, "end": v(-31.67, 79.5) * mm});
            skLineSegment(sketch, "E347", {"start": v(-31.67, 79.5) * mm, "end": v(-32.09, 79.93) * mm});
            skLineSegment(sketch, "E348", {"start": v(-32.09, 79.93) * mm, "end": v(-32.51, 80.26) * mm});
            skLineSegment(sketch, "E349", {"start": v(-32.51, 80.26) * mm, "end": v(-32.94, 80.6) * mm});
            skLineSegment(sketch, "E350", {"start": v(-32.94, 80.6) * mm, "end": v(-33.36, 80.94) * mm});
            skLineSegment(sketch, "E351", {"start": v(-33.36, 80.94) * mm, "end": v(-33.78, 81.2) * mm});
            skLineSegment(sketch, "E352", {"start": v(-33.78, 81.2) * mm, "end": v(-34.3, 81.53) * mm});
            skLineSegment(sketch, "E353", {"start": v(-34.3, 81.53) * mm, "end": v(-34.8, 81.87) * mm});
            skLineSegment(sketch, "E354", {"start": v(-34.8, 81.87) * mm, "end": v(-35.22, 82.13) * mm});
            skLineSegment(sketch, "E355", {"start": v(-35.22, 82.13) * mm, "end": v(-35.73, 82.47) * mm});
            skLineSegment(sketch, "E356", {"start": v(-35.73, 82.47) * mm, "end": v(-36.24, 82.72) * mm});
            skLineSegment(sketch, "E357", {"start": v(-36.24, 82.72) * mm, "end": v(-36.74, 83.06) * mm});
            skLineSegment(sketch, "E358", {"start": v(-36.74, 83.06) * mm, "end": v(-37.25, 83.31) * mm});
            skLineSegment(sketch, "E359", {"start": v(-37.25, 83.31) * mm, "end": v(-37.85, 83.57) * mm});
            skLineSegment(sketch, "E360", {"start": v(-37.85, 83.57) * mm, "end": v(-38.35, 83.82) * mm});
            skLineSegment(sketch, "E361", {"start": v(-38.35, 83.82) * mm, "end": v(-38.95, 84.07) * mm});
            skLineSegment(sketch, "E362", {"start": v(-38.95, 84.07) * mm, "end": v(-39.46, 84.33) * mm});
            skLineSegment(sketch, "E363", {"start": v(-39.46, 84.33) * mm, "end": v(-43.6, 81.28) * mm});
            skLineSegment(sketch, "E364", {"start": v(-43.6, 81.28) * mm, "end": v(-43.52, 80.69) * mm});
            skLineSegment(sketch, "E365", {"start": v(-43.52, 80.69) * mm, "end": v(-43.43, 80.1) * mm});
            skLineSegment(sketch, "E366", {"start": v(-43.43, 80.1) * mm, "end": v(-43.43, 79.5) * mm});
            skLineSegment(sketch, "E367", {"start": v(-43.43, 79.5) * mm, "end": v(-43.26, 78.91) * mm});
            skLineSegment(sketch, "E368", {"start": v(-43.26, 78.91) * mm, "end": v(-43.18, 78.32) * mm});
            skLineSegment(sketch, "E369", {"start": v(-43.18, 78.32) * mm, "end": v(-43.1, 77.72) * mm});
            skLineSegment(sketch, "E370", {"start": v(-43.1, 77.72) * mm, "end": v(-43.01, 77.22) * mm});
            skLineSegment(sketch, "E371", {"start": v(-43.01, 77.22) * mm, "end": v(-42.84, 76.62) * mm});
            skLineSegment(sketch, "E372", {"start": v(-42.84, 76.62) * mm, "end": v(-42.67, 76.12) * mm});
            skLineSegment(sketch, "E373", {"start": v(-42.67, 76.12) * mm, "end": v(-42.59, 75.52) * mm});
            skLineSegment(sketch, "E374", {"start": v(-42.59, 75.52) * mm, "end": v(-42.42, 75.01) * mm});
            skLineSegment(sketch, "E375", {"start": v(-42.42, 75.01) * mm, "end": v(-42.25, 74.42) * mm});
            skLineSegment(sketch, "E376", {"start": v(-42.25, 74.42) * mm, "end": v(-42.08, 73.91) * mm});
            skLineSegment(sketch, "E377", {"start": v(-42.08, 73.91) * mm, "end": v(-41.9, 73.4) * mm});
            skLineSegment(sketch, "E378", {"start": v(-41.9, 73.4) * mm, "end": v(-41.66, 72.9) * mm});
            skLineSegment(sketch, "E379", {"start": v(-41.66, 72.9) * mm, "end": v(-41.49, 72.4) * mm});
            skLineSegment(sketch, "E380", {"start": v(-41.49, 72.4) * mm, "end": v(-41.23, 71.88) * mm});
            skLineSegment(sketch, "E381", {"start": v(-41.23, 71.88) * mm, "end": v(-40.98, 71.46) * mm});
            skLineSegment(sketch, "E382", {"start": v(-40.98, 71.46) * mm, "end": v(-40.81, 70.95) * mm});
            skLineSegment(sketch, "E383", {"start": v(-40.81, 70.95) * mm, "end": v(-40.47, 70.53) * mm});
            skLineSegment(sketch, "E384", {"start": v(-40.47, 70.53) * mm, "end": v(-42.67, 68.41) * mm});
            skLineSegment(sketch, "E385", {"start": v(-42.67, 68.41) * mm, "end": v(-44.79, 66.21) * mm});
            skLineSegment(sketch, "E386", {"start": v(-44.79, 66.21) * mm, "end": v(-45.21, 66.46) * mm});
            skLineSegment(sketch, "E387", {"start": v(-45.21, 66.46) * mm, "end": v(-45.72, 66.72) * mm});
            skLineSegment(sketch, "E388", {"start": v(-45.72, 66.72) * mm, "end": v(-46.23, 66.97) * mm});
            skLineSegment(sketch, "E389", {"start": v(-46.23, 66.97) * mm, "end": v(-46.65, 67.23) * mm});
            skLineSegment(sketch, "E390", {"start": v(-46.65, 67.23) * mm, "end": v(-47.16, 67.4) * mm});
            skLineSegment(sketch, "E391", {"start": v(-47.16, 67.4) * mm, "end": v(-47.67, 67.56) * mm});
            skLineSegment(sketch, "E392", {"start": v(-47.67, 67.56) * mm, "end": v(-48.18, 67.82) * mm});
            skLineSegment(sketch, "E393", {"start": v(-48.18, 67.82) * mm, "end": v(-48.77, 67.99) * mm});
            skLineSegment(sketch, "E394", {"start": v(-48.77, 67.99) * mm, "end": v(-49.28, 68.16) * mm});
            skLineSegment(sketch, "E395", {"start": v(-49.28, 68.16) * mm, "end": v(-49.78, 68.24) * mm});
            skLineSegment(sketch, "E396", {"start": v(-49.78, 68.24) * mm, "end": v(-50.38, 68.41) * mm});
            skLineSegment(sketch, "E397", {"start": v(-50.38, 68.41) * mm, "end": v(-50.88, 68.58) * mm});
            skLineSegment(sketch, "E398", {"start": v(-50.88, 68.58) * mm, "end": v(-51.48, 68.66) * mm});
            skLineSegment(sketch, "E399", {"start": v(-51.48, 68.66) * mm, "end": v(-52.07, 68.83) * mm});
            skLineSegment(sketch, "E400", {"start": v(-52.07, 68.83) * mm, "end": v(-52.66, 68.92) * mm});
            skLineSegment(sketch, "E401", {"start": v(-52.66, 68.92) * mm, "end": v(-53.17, 69) * mm});
            skLineSegment(sketch, "E402", {"start": v(-53.17, 69) * mm, "end": v(-53.76, 69.09) * mm});
            skLineSegment(sketch, "E403", {"start": v(-53.76, 69.09) * mm, "end": v(-54.36, 69.17) * mm});
            skLineSegment(sketch, "E404", {"start": v(-54.36, 69.17) * mm, "end": v(-55.03, 69.26) * mm});
            skLineSegment(sketch, "E405", {"start": v(-55.03, 69.26) * mm, "end": v(-55.63, 69.34) * mm});
            skLineSegment(sketch, "E406", {"start": v(-55.63, 69.34) * mm, "end": v(-58.59, 65.2) * mm});
            skLineSegment(sketch, "E407", {"start": v(-58.59, 65.2) * mm, "end": v(-58.34, 64.6) * mm});
            skLineSegment(sketch, "E408", {"start": v(-58.34, 64.6) * mm, "end": v(-58.08, 64.1) * mm});
            skLineSegment(sketch, "E409", {"start": v(-58.08, 64.1) * mm, "end": v(-57.83, 63.5) * mm});
            skLineSegment(sketch, "E410", {"start": v(-57.83, 63.5) * mm, "end": v(-57.57, 63) * mm});
            skLineSegment(sketch, "E411", {"start": v(-57.57, 63) * mm, "end": v(-57.32, 62.48) * mm});
            skLineSegment(sketch, "E412", {"start": v(-57.32, 62.48) * mm, "end": v(-56.98, 61.98) * mm});
            skLineSegment(sketch, "E413", {"start": v(-56.98, 61.98) * mm, "end": v(-56.73, 61.47) * mm});
            skLineSegment(sketch, "E414", {"start": v(-56.73, 61.47) * mm, "end": v(-56.47, 60.96) * mm});
            skLineSegment(sketch, "E415", {"start": v(-56.47, 60.96) * mm, "end": v(-56.13, 60.45) * mm});
            skLineSegment(sketch, "E416", {"start": v(-56.13, 60.45) * mm, "end": v(-55.8, 60.03) * mm});
            skLineSegment(sketch, "E417", {"start": v(-55.8, 60.03) * mm, "end": v(-55.54, 59.52) * mm});
            skLineSegment(sketch, "E418", {"start": v(-55.54, 59.52) * mm, "end": v(-55.2, 59.1) * mm});
            skLineSegment(sketch, "E419", {"start": v(-55.2, 59.1) * mm, "end": v(-54.86, 58.59) * mm});
            skLineSegment(sketch, "E420", {"start": v(-54.86, 58.59) * mm, "end": v(-54.53, 58.17) * mm});
            skLineSegment(sketch, "E421", {"start": v(-54.53, 58.17) * mm, "end": v(-54.19, 57.74) * mm});
            skLineSegment(sketch, "E422", {"start": v(-54.19, 57.74) * mm, "end": v(-53.85, 57.4) * mm});
            skLineSegment(sketch, "E423", {"start": v(-53.85, 57.4) * mm, "end": v(-53.42, 56.98) * mm});
            skLineSegment(sketch, "E424", {"start": v(-53.42, 56.98) * mm, "end": v(-53.09, 56.56) * mm});
            skLineSegment(sketch, "E425", {"start": v(-53.09, 56.56) * mm, "end": v(-52.75, 56.22) * mm});
            skLineSegment(sketch, "E426", {"start": v(-52.75, 56.22) * mm, "end": v(-52.32, 55.88) * mm});
            skLineSegment(sketch, "E427", {"start": v(-52.32, 55.88) * mm, "end": v(-53.76, 53.17) * mm});
            skLineSegment(sketch, "E428", {"start": v(-53.76, 53.17) * mm, "end": v(-55.03, 50.46) * mm});
            skLineSegment(sketch, "E429", {"start": v(-55.03, 50.46) * mm, "end": v(-55.63, 50.55) * mm});
            skLineSegment(sketch, "E430", {"start": v(-55.63, 50.55) * mm, "end": v(-56.13, 50.63) * mm});
            skLineSegment(sketch, "E431", {"start": v(-56.13, 50.63) * mm, "end": v(-56.64, 50.72) * mm});
            skLineSegment(sketch, "E432", {"start": v(-56.64, 50.72) * mm, "end": v(-57.15, 50.8) * mm});
            skLineSegment(sketch, "E433", {"start": v(-57.15, 50.8) * mm, "end": v(-57.74, 50.8) * mm});
            skLineSegment(sketch, "E434", {"start": v(-57.74, 50.8) * mm, "end": v(-58.25, 50.88) * mm});
            skLineSegment(sketch, "E435", {"start": v(-58.25, 50.88) * mm, "end": v(-58.84, 50.88) * mm});
            skLineSegment(sketch, "E436", {"start": v(-58.84, 50.88) * mm, "end": v(-59.35, 50.88) * mm});
            skLineSegment(sketch, "E437", {"start": v(-59.35, 50.88) * mm, "end": v(-59.94, 50.88) * mm});
            skLineSegment(sketch, "E438", {"start": v(-59.94, 50.88) * mm, "end": v(-60.45, 50.88) * mm});
            skLineSegment(sketch, "E439", {"start": v(-60.45, 50.88) * mm, "end": v(-61.05, 50.8) * mm});
            skLineSegment(sketch, "E440", {"start": v(-61.05, 50.8) * mm, "end": v(-61.64, 50.8) * mm});
            skLineSegment(sketch, "E441", {"start": v(-61.64, 50.8) * mm, "end": v(-62.14, 50.72) * mm});
            skLineSegment(sketch, "E442", {"start": v(-62.14, 50.72) * mm, "end": v(-62.74, 50.72) * mm});
            skLineSegment(sketch, "E443", {"start": v(-62.74, 50.72) * mm, "end": v(-63.33, 50.63) * mm});
            skLineSegment(sketch, "E444", {"start": v(-63.33, 50.63) * mm, "end": v(-63.92, 50.55) * mm});
            skLineSegment(sketch, "E445", {"start": v(-63.92, 50.55) * mm, "end": v(-64.52, 50.38) * mm});
            skLineSegment(sketch, "E446", {"start": v(-64.52, 50.38) * mm, "end": v(-65.1, 50.3) * mm});
            skLineSegment(sketch, "E447", {"start": v(-65.1, 50.3) * mm, "end": v(-65.7, 50.2) * mm});
            skLineSegment(sketch, "E448", {"start": v(-65.7, 50.2) * mm, "end": v(-66.3, 50.04) * mm});
            skLineSegment(sketch, "E449", {"start": v(-66.3, 50.04) * mm, "end": v(-67.9, 45.21) * mm});
            skLineSegment(sketch, "E450", {"start": v(-67.9, 45.21) * mm, "end": v(-67.48, 44.7) * mm});
            skLineSegment(sketch, "E451", {"start": v(-67.48, 44.7) * mm, "end": v(-67.06, 44.28) * mm});
            skLineSegment(sketch, "E452", {"start": v(-67.06, 44.28) * mm, "end": v(-66.63, 43.86) * mm});
            skLineSegment(sketch, "E453", {"start": v(-66.63, 43.86) * mm, "end": v(-66.21, 43.43) * mm});
            skLineSegment(sketch, "E454", {"start": v(-66.21, 43.43) * mm, "end": v(-65.79, 43.01) * mm});
            skLineSegment(sketch, "E455", {"start": v(-65.79, 43.01) * mm, "end": v(-65.36, 42.67) * mm});
            skLineSegment(sketch, "E456", {"start": v(-65.36, 42.67) * mm, "end": v(-64.94, 42.25) * mm});
            skLineSegment(sketch, "E457", {"start": v(-64.94, 42.25) * mm, "end": v(-64.52, 41.83) * mm});
            skLineSegment(sketch, "E458", {"start": v(-64.52, 41.83) * mm, "end": v(-64.1, 41.49) * mm});
            skLineSegment(sketch, "E459", {"start": v(-64.1, 41.49) * mm, "end": v(-63.67, 41.15) * mm});
            skLineSegment(sketch, "E460", {"start": v(-63.67, 41.15) * mm, "end": v(-63.16, 40.81) * mm});
            skLineSegment(sketch, "E461", {"start": v(-63.16, 40.81) * mm, "end": v(-62.74, 40.47) * mm});
            skLineSegment(sketch, "E462", {"start": v(-62.74, 40.47) * mm, "end": v(-62.31, 40.13) * mm});
            skLineSegment(sketch, "E463", {"start": v(-62.31, 40.13) * mm, "end": v(-61.8, 39.8) * mm});
            skLineSegment(sketch, "E464", {"start": v(-61.8, 39.8) * mm, "end": v(-61.38, 39.54) * mm});
            skLineSegment(sketch, "E465", {"start": v(-61.38, 39.54) * mm, "end": v(-60.96, 39.2) * mm});
            skLineSegment(sketch, "E466", {"start": v(-60.96, 39.2) * mm, "end": v(-60.45, 38.95) * mm});
            skLineSegment(sketch, "E467", {"start": v(-60.45, 38.95) * mm, "end": v(-59.94, 38.78) * mm});
            skLineSegment(sketch, "E468", {"start": v(-59.94, 38.78) * mm, "end": v(-59.52, 38.52) * mm});
            skLineSegment(sketch, "E469", {"start": v(-59.52, 38.52) * mm, "end": v(-59.01, 38.27) * mm});
            skLineSegment(sketch, "E470", {"start": v(-59.01, 38.27) * mm, "end": v(-59.6, 35.3) * mm});
            skLineSegment(sketch, "E471", {"start": v(-59.6, 35.3) * mm, "end": v(-59.94, 32.26) * mm});
            skLineSegment(sketch, "E472", {"start": v(-59.94, 32.26) * mm, "end": v(-60.54, 32.26) * mm});
            skLineSegment(sketch, "E473", {"start": v(-60.54, 32.26) * mm, "end": v(-61.05, 32.17) * mm});
            skLineSegment(sketch, "E474", {"start": v(-61.05, 32.17) * mm, "end": v(-61.55, 32.09) * mm});
            skLineSegment(sketch, "E475", {"start": v(-61.55, 32.09) * mm, "end": v(-62.06, 32) * mm});
            skLineSegment(sketch, "E476", {"start": v(-62.06, 32) * mm, "end": v(-62.65, 31.83) * mm});
            skLineSegment(sketch, "E477", {"start": v(-62.65, 31.83) * mm, "end": v(-63.16, 31.67) * mm});
            skLineSegment(sketch, "E478", {"start": v(-63.16, 31.67) * mm, "end": v(-63.67, 31.58) * mm});
            skLineSegment(sketch, "E479", {"start": v(-63.67, 31.58) * mm, "end": v(-64.18, 31.41) * mm});
            skLineSegment(sketch, "E480", {"start": v(-64.18, 31.41) * mm, "end": v(-64.69, 31.16) * mm});
            skLineSegment(sketch, "E481", {"start": v(-64.69, 31.16) * mm, "end": v(-65.28, 30.99) * mm});
            skLineSegment(sketch, "E482", {"start": v(-65.28, 30.99) * mm, "end": v(-65.79, 30.82) * mm});
            skLineSegment(sketch, "E483", {"start": v(-65.79, 30.82) * mm, "end": v(-66.3, 30.56) * mm});
            skLineSegment(sketch, "E484", {"start": v(-66.3, 30.56) * mm, "end": v(-66.8, 30.4) * mm});
            skLineSegment(sketch, "E485", {"start": v(-66.8, 30.4) * mm, "end": v(-67.4, 30.14) * mm});
            skLineSegment(sketch, "E486", {"start": v(-67.4, 30.14) * mm, "end": v(-67.9, 29.89) * mm});
            skLineSegment(sketch, "E487", {"start": v(-67.9, 29.89) * mm, "end": v(-68.41, 29.63) * mm});
            skLineSegment(sketch, "E488", {"start": v(-68.41, 29.63) * mm, "end": v(-68.92, 29.38) * mm});
            skLineSegment(sketch, "E489", {"start": v(-68.92, 29.38) * mm, "end": v(-69.51, 29.04) * mm});
            skLineSegment(sketch, "E490", {"start": v(-69.51, 29.04) * mm, "end": v(-70.02, 28.79) * mm});
            skLineSegment(sketch, "E491", {"start": v(-70.02, 28.79) * mm, "end": v(-70.53, 28.45) * mm});
            skLineSegment(sketch, "E492", {"start": v(-70.53, 28.45) * mm, "end": v(-70.53, 23.37) * mm});
            skLineSegment(sketch, "E493", {"start": v(-70.53, 23.37) * mm, "end": v(-70.02, 23.03) * mm});
            skLineSegment(sketch, "E494", {"start": v(-70.02, 23.03) * mm, "end": v(-69.51, 22.7) * mm});
            skLineSegment(sketch, "E495", {"start": v(-69.51, 22.7) * mm, "end": v(-68.92, 22.44) * mm});
            skLineSegment(sketch, "E496", {"start": v(-68.92, 22.44) * mm, "end": v(-68.41, 22.18) * mm});
            skLineSegment(sketch, "E497", {"start": v(-68.41, 22.18) * mm, "end": v(-67.9, 21.93) * mm});
            skLineSegment(sketch, "E498", {"start": v(-67.9, 21.93) * mm, "end": v(-67.4, 21.67) * mm});
            skLineSegment(sketch, "E499", {"start": v(-67.4, 21.67) * mm, "end": v(-66.8, 21.42) * mm});
            skLineSegment(sketch, "E500", {"start": v(-66.8, 21.42) * mm, "end": v(-66.3, 21.17) * mm});
            skLineSegment(sketch, "E501", {"start": v(-66.3, 21.17) * mm, "end": v(-65.79, 21) * mm});
            skLineSegment(sketch, "E502", {"start": v(-65.79, 21) * mm, "end": v(-65.28, 20.74) * mm});
            skLineSegment(sketch, "E503", {"start": v(-65.28, 20.74) * mm, "end": v(-64.69, 20.57) * mm});
            skLineSegment(sketch, "E504", {"start": v(-64.69, 20.57) * mm, "end": v(-64.18, 20.4) * mm});
            skLineSegment(sketch, "E505", {"start": v(-64.18, 20.4) * mm, "end": v(-63.67, 20.24) * mm});
            skLineSegment(sketch, "E506", {"start": v(-63.67, 20.24) * mm, "end": v(-63.16, 20.07) * mm});
            skLineSegment(sketch, "E507", {"start": v(-63.16, 20.07) * mm, "end": v(-62.65, 19.98) * mm});
            skLineSegment(sketch, "E508", {"start": v(-62.65, 19.98) * mm, "end": v(-62.06, 19.81) * mm});
            skLineSegment(sketch, "E509", {"start": v(-62.06, 19.81) * mm, "end": v(-61.55, 19.73) * mm});
            skLineSegment(sketch, "E510", {"start": v(-61.55, 19.73) * mm, "end": v(-61.05, 19.64) * mm});
            skLineSegment(sketch, "E511", {"start": v(-61.05, 19.64) * mm, "end": v(-60.54, 19.56) * mm});
            skLineSegment(sketch, "E512", {"start": v(-60.54, 19.56) * mm, "end": v(-59.94, 19.47) * mm});
            skLineSegment(sketch, "E513", {"start": v(-59.94, 19.47) * mm, "end": v(-59.6, 16.5) * mm});
            skLineSegment(sketch, "E514", {"start": v(-59.6, 16.5) * mm, "end": v(-59.01, 13.46) * mm});
            skLineSegment(sketch, "E515", {"start": v(-59.01, 13.46) * mm, "end": v(-59.52, 13.3) * mm});
            skLineSegment(sketch, "E516", {"start": v(-59.52, 13.3) * mm, "end": v(-59.94, 13.04) * mm});
            skLineSegment(sketch, "E517", {"start": v(-59.94, 13.04) * mm, "end": v(-60.45, 12.78) * mm});
            skLineSegment(sketch, "E518", {"start": v(-60.45, 12.78) * mm, "end": v(-60.96, 12.53) * mm});
            skLineSegment(sketch, "E519", {"start": v(-60.96, 12.53) * mm, "end": v(-61.38, 12.28) * mm});
            skLineSegment(sketch, "E520", {"start": v(-61.38, 12.28) * mm, "end": v(-61.8, 11.94) * mm});
            skLineSegment(sketch, "E521", {"start": v(-61.8, 11.94) * mm, "end": v(-62.31, 11.68) * mm});
            skLineSegment(sketch, "E522", {"start": v(-62.31, 11.68) * mm, "end": v(-62.74, 11.34) * mm});
            skLineSegment(sketch, "E523", {"start": v(-62.74, 11.34) * mm, "end": v(-63.16, 11) * mm});
            skLineSegment(sketch, "E524", {"start": v(-63.16, 11) * mm, "end": v(-63.67, 10.67) * mm});
            skLineSegment(sketch, "E525", {"start": v(-63.67, 10.67) * mm, "end": v(-64.1, 10.25) * mm});
            skLineSegment(sketch, "E526", {"start": v(-64.1, 10.25) * mm, "end": v(-64.52, 9.9) * mm});
            skLineSegment(sketch, "E527", {"start": v(-64.52, 9.9) * mm, "end": v(-64.94, 9.57) * mm});
            skLineSegment(sketch, "E528", {"start": v(-64.94, 9.57) * mm, "end": v(-65.36, 9.14) * mm});
            skLineSegment(sketch, "E529", {"start": v(-65.36, 9.14) * mm, "end": v(-65.79, 8.72) * mm});
            skLineSegment(sketch, "E530", {"start": v(-65.79, 8.72) * mm, "end": v(-66.21, 8.3) * mm});
            skLineSegment(sketch, "E531", {"start": v(-66.21, 8.3) * mm, "end": v(-66.63, 7.87) * mm});
            skLineSegment(sketch, "E532", {"start": v(-66.63, 7.87) * mm, "end": v(-67.06, 7.45) * mm});
            skLineSegment(sketch, "E533", {"start": v(-67.06, 7.45) * mm, "end": v(-67.48, 7.03) * mm});
            skLineSegment(sketch, "E534", {"start": v(-67.48, 7.03) * mm, "end": v(-67.9, 6.6) * mm});
            skLineSegment(sketch, "E535", {"start": v(-67.9, 6.6) * mm, "end": v(-66.3, 1.7) * mm});
            skLineSegment(sketch, "E536", {"start": v(-66.3, 1.7) * mm, "end": v(-65.7, 1.6) * mm});
            skLineSegment(sketch, "E537", {"start": v(-65.7, 1.6) * mm, "end": v(-65.1, 1.44) * mm});
            skLineSegment(sketch, "E538", {"start": v(-65.1, 1.44) * mm, "end": v(-64.52, 1.36) * mm});
            skLineSegment(sketch, "E539", {"start": v(-64.52, 1.36) * mm, "end": v(-63.92, 1.27) * mm});
            skLineSegment(sketch, "E540", {"start": v(-63.92, 1.27) * mm, "end": v(-63.33, 1.19) * mm});
            skLineSegment(sketch, "E541", {"start": v(-63.33, 1.19) * mm, "end": v(-62.74, 1.1) * mm});
            skLineSegment(sketch, "E542", {"start": v(-62.74, 1.1) * mm, "end": v(-62.14, 1.02) * mm});
            skLineSegment(sketch, "E543", {"start": v(-62.14, 1.02) * mm, "end": v(-61.64, 1.02) * mm});
            skLineSegment(sketch, "E544", {"start": v(-61.64, 1.02) * mm, "end": v(-61.05, 0.93) * mm});
            skLineSegment(sketch, "E545", {"start": v(-61.05, 0.93) * mm, "end": v(-60.45, 0.93) * mm});
            skLineSegment(sketch, "E546", {"start": v(-60.45, 0.93) * mm, "end": v(-59.94, 0.85) * mm});
            skLineSegment(sketch, "E547", {"start": v(-59.94, 0.85) * mm, "end": v(-59.35, 0.85) * mm});
            skLineSegment(sketch, "E548", {"start": v(-59.35, 0.85) * mm, "end": v(-58.84, 0.85) * mm});
            skLineSegment(sketch, "E549", {"start": v(-58.84, 0.85) * mm, "end": v(-58.25, 0.93) * mm});
            skLineSegment(sketch, "E550", {"start": v(-58.25, 0.93) * mm, "end": v(-57.74, 0.93) * mm});
            skLineSegment(sketch, "E551", {"start": v(-57.74, 0.93) * mm, "end": v(-57.15, 1.02) * mm});
            skLineSegment(sketch, "E552", {"start": v(-57.15, 1.02) * mm, "end": v(-56.64, 1.02) * mm});
            skLineSegment(sketch, "E553", {"start": v(-56.64, 1.02) * mm, "end": v(-56.13, 1.1) * mm});
            skLineSegment(sketch, "E554", {"start": v(-56.13, 1.1) * mm, "end": v(-55.63, 1.19) * mm});
            skLineSegment(sketch, "E555", {"start": v(-55.63, 1.19) * mm, "end": v(-55.03, 1.36) * mm});
            skLineSegment(sketch, "E556", {"start": v(-55.03, 1.36) * mm, "end": v(-53.76, -1.44) * mm});
            skLineSegment(sketch, "E557", {"start": v(-53.76, -1.44) * mm, "end": v(-52.32, -4.06) * mm});
            skLineSegment(sketch, "E558", {"start": v(-52.32, -4.06) * mm, "end": v(-52.75, -4.49) * mm});
            skLineSegment(sketch, "E559", {"start": v(-52.75, -4.49) * mm, "end": v(-53.09, -4.83) * mm});
            skLineSegment(sketch, "E560", {"start": v(-53.09, -4.83) * mm, "end": v(-53.42, -5.16) * mm});
            skLineSegment(sketch, "E561", {"start": v(-53.42, -5.16) * mm, "end": v(-53.85, -5.59) * mm});
            skLineSegment(sketch, "E562", {"start": v(-53.85, -5.59) * mm, "end": v(-54.19, -6.01) * mm});
            skLineSegment(sketch, "E563", {"start": v(-54.19, -6.01) * mm, "end": v(-54.53, -6.43) * mm});
            skLineSegment(sketch, "E564", {"start": v(-54.53, -6.43) * mm, "end": v(-54.86, -6.86) * mm});
            skLineSegment(sketch, "E565", {"start": v(-54.86, -6.86) * mm, "end": v(-55.2, -7.28) * mm});
            skLineSegment(sketch, "E566", {"start": v(-55.2, -7.28) * mm, "end": v(-55.54, -7.79) * mm});
            skLineSegment(sketch, "E567", {"start": v(-55.54, -7.79) * mm, "end": v(-55.8, -8.21) * mm});
            skLineSegment(sketch, "E568", {"start": v(-55.8, -8.21) * mm, "end": v(-56.13, -8.72) * mm});
            skLineSegment(sketch, "E569", {"start": v(-56.13, -8.72) * mm, "end": v(-56.47, -9.14) * mm});
            skLineSegment(sketch, "E570", {"start": v(-56.47, -9.14) * mm, "end": v(-56.73, -9.65) * mm});
            skLineSegment(sketch, "E571", {"start": v(-56.73, -9.65) * mm, "end": v(-56.98, -10.16) * mm});
            skLineSegment(sketch, "E572", {"start": v(-56.98, -10.16) * mm, "end": v(-57.32, -10.67) * mm});
            skLineSegment(sketch, "E573", {"start": v(-57.32, -10.67) * mm, "end": v(-57.57, -11.18) * mm});
            skLineSegment(sketch, "E574", {"start": v(-57.57, -11.18) * mm, "end": v(-57.83, -11.77) * mm});
            skLineSegment(sketch, "E575", {"start": v(-57.83, -11.77) * mm, "end": v(-58.08, -12.28) * mm});
            skLineSegment(sketch, "E576", {"start": v(-58.08, -12.28) * mm, "end": v(-58.34, -12.87) * mm});
            skLineSegment(sketch, "E577", {"start": v(-58.34, -12.87) * mm, "end": v(-58.59, -13.38) * mm});
            skLineSegment(sketch, "E578", {"start": v(-58.59, -13.38) * mm, "end": v(-55.63, -17.53) * mm});
            skLineSegment(sketch, "E579", {"start": v(-55.63, -17.53) * mm, "end": v(-55.03, -17.44) * mm});
            skLineSegment(sketch, "E580", {"start": v(-55.03, -17.44) * mm, "end": v(-54.36, -17.36) * mm});
            skLineSegment(sketch, "E581", {"start": v(-54.36, -17.36) * mm, "end": v(-53.76, -17.36) * mm});
            skLineSegment(sketch, "E582", {"start": v(-53.76, -17.36) * mm, "end": v(-53.17, -17.27) * mm});
            skLineSegment(sketch, "E583", {"start": v(-53.17, -17.27) * mm, "end": v(-52.66, -17.1) * mm});
            skLineSegment(sketch, "E584", {"start": v(-52.66, -17.1) * mm, "end": v(-52.07, -17.02) * mm});
            skLineSegment(sketch, "E585", {"start": v(-52.07, -17.02) * mm, "end": v(-51.48, -16.93) * mm});
            skLineSegment(sketch, "E586", {"start": v(-51.48, -16.93) * mm, "end": v(-50.88, -16.76) * mm});
            skLineSegment(sketch, "E587", {"start": v(-50.88, -16.76) * mm, "end": v(-50.38, -16.68) * mm});
            skLineSegment(sketch, "E588", {"start": v(-50.38, -16.68) * mm, "end": v(-49.78, -16.5) * mm});
            skLineSegment(sketch, "E589", {"start": v(-49.78, -16.5) * mm, "end": v(-49.28, -16.34) * mm});
            skLineSegment(sketch, "E590", {"start": v(-49.28, -16.34) * mm, "end": v(-48.77, -16.17) * mm});
            skLineSegment(sketch, "E591", {"start": v(-48.77, -16.17) * mm, "end": v(-48.18, -16) * mm});
            skLineSegment(sketch, "E592", {"start": v(-48.18, -16) * mm, "end": v(-47.67, -15.83) * mm});
            skLineSegment(sketch, "E593", {"start": v(-47.67, -15.83) * mm, "end": v(-47.16, -15.58) * mm});
            skLineSegment(sketch, "E594", {"start": v(-47.16, -15.58) * mm, "end": v(-46.65, -15.4) * mm});
            skLineSegment(sketch, "E595", {"start": v(-46.65, -15.4) * mm, "end": v(-46.23, -15.15) * mm});
            skLineSegment(sketch, "E596", {"start": v(-46.23, -15.15) * mm, "end": v(-45.72, -14.99) * mm});
            skLineSegment(sketch, "E597", {"start": v(-45.72, -14.99) * mm, "end": v(-45.21, -14.73) * mm});
            skLineSegment(sketch, "E598", {"start": v(-45.21, -14.73) * mm, "end": v(-44.79, -14.48) * mm});
            skLineSegment(sketch, "E599", {"start": v(-44.79, -14.48) * mm, "end": v(-42.67, -16.68) * mm});
            skLineSegment(sketch, "E600", {"start": v(-42.67, -16.68) * mm, "end": v(-40.47, -18.71) * mm});
            skLineSegment(sketch, "E601", {"start": v(-40.47, -18.71) * mm, "end": v(-40.81, -19.22) * mm});
            skLineSegment(sketch, "E602", {"start": v(-40.81, -19.22) * mm, "end": v(-40.98, -19.64) * mm});
            skLineSegment(sketch, "E603", {"start": v(-40.98, -19.64) * mm, "end": v(-41.23, -20.15) * mm});
            skLineSegment(sketch, "E604", {"start": v(-41.23, -20.15) * mm, "end": v(-41.49, -20.66) * mm});
            skLineSegment(sketch, "E605", {"start": v(-41.49, -20.66) * mm, "end": v(-41.66, -21.08) * mm});
            skLineSegment(sketch, "E606", {"start": v(-41.66, -21.08) * mm, "end": v(-41.9, -21.67) * mm});
            skLineSegment(sketch, "E607", {"start": v(-41.9, -21.67) * mm, "end": v(-42.08, -22.18) * mm});
            skLineSegment(sketch, "E608", {"start": v(-42.08, -22.18) * mm, "end": v(-42.25, -22.69) * mm});
            skLineSegment(sketch, "E609", {"start": v(-42.25, -22.69) * mm, "end": v(-42.42, -23.2) * mm});
            skLineSegment(sketch, "E610", {"start": v(-42.42, -23.2) * mm, "end": v(-42.59, -23.7) * mm});
            skLineSegment(sketch, "E611", {"start": v(-42.59, -23.7) * mm, "end": v(-42.67, -24.3) * mm});
            skLineSegment(sketch, "E612", {"start": v(-42.67, -24.3) * mm, "end": v(-42.84, -24.9) * mm});
            skLineSegment(sketch, "E613", {"start": v(-42.84, -24.9) * mm, "end": v(-43.01, -25.4) * mm});
            skLineSegment(sketch, "E614", {"start": v(-43.01, -25.4) * mm, "end": v(-43.1, -26) * mm});
            skLineSegment(sketch, "E615", {"start": v(-43.1, -26) * mm, "end": v(-43.18, -26.59) * mm});
            skLineSegment(sketch, "E616", {"start": v(-43.18, -26.59) * mm, "end": v(-43.26, -27.18) * mm});
            skLineSegment(sketch, "E617", {"start": v(-43.26, -27.18) * mm, "end": v(-43.43, -27.69) * mm});
            skLineSegment(sketch, "E618", {"start": v(-43.43, -27.69) * mm, "end": v(-43.43, -28.36) * mm});
            skLineSegment(sketch, "E619", {"start": v(-43.43, -28.36) * mm, "end": v(-43.52, -28.96) * mm});
            skLineSegment(sketch, "E620", {"start": v(-43.52, -28.96) * mm, "end": v(-43.6, -29.55) * mm});
            skLineSegment(sketch, "E621", {"start": v(-43.6, -29.55) * mm, "end": v(-39.46, -32.51) * mm});
            skLineSegment(sketch, "E622", {"start": v(-39.46, -32.51) * mm, "end": v(-38.95, -32.26) * mm});
            skLineSegment(sketch, "E623", {"start": v(-38.95, -32.26) * mm, "end": v(-38.35, -32.09) * mm});
            skLineSegment(sketch, "E624", {"start": v(-38.35, -32.09) * mm, "end": v(-37.85, -31.75) * mm});
            skLineSegment(sketch, "E625", {"start": v(-37.85, -31.75) * mm, "end": v(-37.25, -31.5) * mm});
            skLineSegment(sketch, "E626", {"start": v(-37.25, -31.5) * mm, "end": v(-36.74, -31.24) * mm});
            skLineSegment(sketch, "E627", {"start": v(-36.74, -31.24) * mm, "end": v(-36.24, -30.99) * mm});
            skLineSegment(sketch, "E628", {"start": v(-36.24, -30.99) * mm, "end": v(-35.73, -30.65) * mm});
            skLineSegment(sketch, "E629", {"start": v(-35.73, -30.65) * mm, "end": v(-35.22, -30.4) * mm});
            skLineSegment(sketch, "E630", {"start": v(-35.22, -30.4) * mm, "end": v(-34.8, -30.06) * mm});
            skLineSegment(sketch, "E631", {"start": v(-34.8, -30.06) * mm, "end": v(-34.3, -29.8) * mm});
            skLineSegment(sketch, "E632", {"start": v(-34.3, -29.8) * mm, "end": v(-33.78, -29.46) * mm});
            skLineSegment(sketch, "E633", {"start": v(-33.78, -29.46) * mm, "end": v(-33.36, -29.13) * mm});
            skLineSegment(sketch, "E634", {"start": v(-33.36, -29.13) * mm, "end": v(-32.94, -28.79) * mm});
            skLineSegment(sketch, "E635", {"start": v(-32.94, -28.79) * mm, "end": v(-32.51, -28.45) * mm});
            skLineSegment(sketch, "E636", {"start": v(-32.51, -28.45) * mm, "end": v(-32.09, -28.1) * mm});
            skLineSegment(sketch, "E637", {"start": v(-32.09, -28.1) * mm, "end": v(-31.67, -27.77) * mm});
            skLineSegment(sketch, "E638", {"start": v(-31.67, -27.77) * mm, "end": v(-31.24, -27.43) * mm});
            skLineSegment(sketch, "E639", {"start": v(-31.24, -27.43) * mm, "end": v(-30.9, -27) * mm});
            skLineSegment(sketch, "E640", {"start": v(-30.9, -27) * mm, "end": v(-30.48, -26.67) * mm});
            skLineSegment(sketch, "E641", {"start": v(-30.48, -26.67) * mm, "end": v(-30.14, -26.25) * mm});
            skLineSegment(sketch, "E642", {"start": v(-30.14, -26.25) * mm, "end": v(-27.52, -27.69) * mm});
            skLineSegment(sketch, "E643", {"start": v(-27.52, -27.69) * mm, "end": v(-24.72, -29.04) * mm});
            skLineSegment(sketch, "E644", {"start": v(-24.72, -29.04) * mm, "end": v(-24.8, -29.55) * mm});
            skLineSegment(sketch, "E645", {"start": v(-24.8, -29.55) * mm, "end": v(-24.98, -30.06) * mm});
            skLineSegment(sketch, "E646", {"start": v(-24.98, -30.06) * mm, "end": v(-24.98, -30.56) * mm});
            skLineSegment(sketch, "E647", {"start": v(-24.98, -30.56) * mm, "end": v(-25.06, -31.16) * mm});
            skLineSegment(sketch, "E648", {"start": v(-25.06, -31.16) * mm, "end": v(-25.15, -31.67) * mm});
            skLineSegment(sketch, "E649", {"start": v(-25.15, -31.67) * mm, "end": v(-25.15, -32.17) * mm});
            skLineSegment(sketch, "E650", {"start": v(-25.15, -32.17) * mm, "end": v(-25.15, -32.77) * mm});
            skLineSegment(sketch, "E651", {"start": v(-25.15, -32.77) * mm, "end": v(-25.15, -33.27) * mm});
            skLineSegment(sketch, "E652", {"start": v(-25.15, -33.27) * mm, "end": v(-25.15, -33.87) * mm});
            skLineSegment(sketch, "E653", {"start": v(-25.15, -33.87) * mm, "end": v(-25.15, -34.46) * mm});
            skLineSegment(sketch, "E654", {"start": v(-25.15, -34.46) * mm, "end": v(-25.15, -34.97) * mm});
            skLineSegment(sketch, "E655", {"start": v(-25.15, -34.97) * mm, "end": v(-25.06, -35.56) * mm});
            skLineSegment(sketch, "E656", {"start": v(-25.06, -35.56) * mm, "end": v(-25.06, -36.15) * mm});
            skLineSegment(sketch, "E657", {"start": v(-25.06, -36.15) * mm, "end": v(-24.98, -36.74) * mm});
            skLineSegment(sketch, "E658", {"start": v(-24.98, -36.74) * mm, "end": v(-24.9, -37.25) * mm});
            skLineSegment(sketch, "E659", {"start": v(-24.9, -37.25) * mm, "end": v(-24.8, -37.85) * mm});
            skLineSegment(sketch, "E660", {"start": v(-24.8, -37.85) * mm, "end": v(-24.72, -38.44) * mm});
            skLineSegment(sketch, "E661", {"start": v(-24.72, -38.44) * mm, "end": v(-24.64, -39.03) * mm});
            skLineSegment(sketch, "E662", {"start": v(-24.64, -39.03) * mm, "end": v(-24.47, -39.62) * mm});
            skLineSegment(sketch, "E663", {"start": v(-24.47, -39.62) * mm, "end": v(-24.3, -40.22) * mm});
            skLineSegment(sketch, "E664", {"start": v(-24.3, -40.22) * mm, "end": v(-19.47, -41.83) * mm});
            skLineSegment(sketch, "E665", {"start": v(-19.47, -41.83) * mm, "end": v(-19.05, -41.4) * mm});
            skLineSegment(sketch, "E666", {"start": v(-19.05, -41.4) * mm, "end": v(-18.54, -40.98) * mm});
            skLineSegment(sketch, "E667", {"start": v(-18.54, -40.98) * mm, "end": v(-18.12, -40.55) * mm});
            skLineSegment(sketch, "E668", {"start": v(-18.12, -40.55) * mm, "end": v(-17.7, -40.13) * mm});
            skLineSegment(sketch, "E669", {"start": v(-17.7, -40.13) * mm, "end": v(-17.27, -39.7) * mm});
            skLineSegment(sketch, "E670", {"start": v(-17.27, -39.7) * mm, "end": v(-16.93, -39.29) * mm});
            skLineSegment(sketch, "E671", {"start": v(-16.93, -39.29) * mm, "end": v(-16.5, -38.86) * mm});
            skLineSegment(sketch, "E672", {"start": v(-16.5, -38.86) * mm, "end": v(-16.17, -38.44) * mm});
            skLineSegment(sketch, "E673", {"start": v(-16.17, -38.44) * mm, "end": v(-15.75, -38.02) * mm});
            skLineSegment(sketch, "E674", {"start": v(-15.75, -38.02) * mm, "end": v(-15.41, -37.6) * mm});
            skLineSegment(sketch, "E675", {"start": v(-15.41, -37.6) * mm, "end": v(-15.07, -37.17) * mm});
            skLineSegment(sketch, "E676", {"start": v(-15.07, -37.17) * mm, "end": v(-14.73, -36.66) * mm});
            skLineSegment(sketch, "E677", {"start": v(-14.73, -36.66) * mm, "end": v(-14.4, -36.24) * mm});
            skLineSegment(sketch, "E678", {"start": v(-14.4, -36.24) * mm, "end": v(-14.06, -35.81) * mm});
            skLineSegment(sketch, "E679", {"start": v(-14.06, -35.81) * mm, "end": v(-13.8, -35.3) * mm});
            skLineSegment(sketch, "E680", {"start": v(-13.8, -35.3) * mm, "end": v(-13.55, -34.88) * mm});
            skLineSegment(sketch, "E681", {"start": v(-13.55, -34.88) * mm, "end": v(-13.3, -34.37) * mm});
            skLineSegment(sketch, "E682", {"start": v(-13.3, -34.37) * mm, "end": v(-13.04, -33.95) * mm});
            skLineSegment(sketch, "E683", {"start": v(-13.04, -33.95) * mm, "end": v(-12.78, -33.44) * mm});
            skLineSegment(sketch, "E684", {"start": v(-12.78, -33.44) * mm, "end": v(-12.62, -33.02) * mm});
            skLineSegment(sketch, "E685", {"start": v(-12.62, -33.02) * mm, "end": v(-9.57, -33.53) * mm});
            skLineSegment(sketch, "E686", {"start": v(-9.57, -33.53) * mm, "end": v(-6.52, -33.95) * mm});
            skLineSegment(sketch, "E687", {"start": v(-6.52, -33.95) * mm, "end": v(-6.52, -34.46) * mm});
            skLineSegment(sketch, "E688", {"start": v(-6.52, -34.46) * mm, "end": v(-6.43, -34.97) * mm});
            skLineSegment(sketch, "E689", {"start": v(-6.43, -34.97) * mm, "end": v(-6.35, -35.48) * mm});
            skLineSegment(sketch, "E690", {"start": v(-6.35, -35.48) * mm, "end": v(-6.27, -35.98) * mm});
            skLineSegment(sketch, "E691", {"start": v(-6.27, -35.98) * mm, "end": v(-6.1, -36.58) * mm});
            skLineSegment(sketch, "E692", {"start": v(-6.1, -36.58) * mm, "end": v(-6.01, -37.08) * mm});
            skLineSegment(sketch, "E693", {"start": v(-6.01, -37.08) * mm, "end": v(-5.84, -37.6) * mm});
            skLineSegment(sketch, "E694", {"start": v(-5.84, -37.6) * mm, "end": v(-5.67, -38.1) * mm});
            skLineSegment(sketch, "E695", {"start": v(-5.67, -38.1) * mm, "end": v(-5.5, -38.7) * mm});
            skLineSegment(sketch, "E696", {"start": v(-5.5, -38.7) * mm, "end": v(-5.25, -39.2) * mm});
            skLineSegment(sketch, "E697", {"start": v(-5.25, -39.2) * mm, "end": v(-5.08, -39.7) * mm});
            skLineSegment(sketch, "E698", {"start": v(-5.08, -39.7) * mm, "end": v(-4.91, -40.22) * mm});
            skLineSegment(sketch, "E699", {"start": v(-4.91, -40.22) * mm, "end": v(-4.66, -40.8) * mm});
            skLineSegment(sketch, "E700", {"start": v(-4.66, -40.8) * mm, "end": v(-4.4, -41.32) * mm});
            skLineSegment(sketch, "E701", {"start": v(-4.4, -41.32) * mm, "end": v(-4.15, -41.83) * mm});
            skLineSegment(sketch, "E702", {"start": v(-4.15, -41.83) * mm, "end": v(-3.9, -42.33) * mm});
            skLineSegment(sketch, "E703", {"start": v(-3.9, -42.33) * mm, "end": v(-3.64, -42.93) * mm});
            skLineSegment(sketch, "E704", {"start": v(-3.64, -42.93) * mm, "end": v(-3.3, -43.43) * mm});
            skLineSegment(sketch, "E705", {"start": v(-3.3, -43.43) * mm, "end": v(-3.05, -43.94) * mm});
            skLineSegment(sketch, "E706", {"start": v(-3.05, -43.94) * mm, "end": v(-2.71, -44.45) * mm});
            skLineSegment(sketch, "E707", {"start": v(-2.71, -44.45) * mm, "end": v(2.37, -44.45) * mm});
            skLineSegment(sketch, "E708", {"start": v(2.37, -44.45) * mm, "end": v(2.7, -43.94) * mm});
            skLineSegment(sketch, "E709", {"start": v(2.7, -43.94) * mm, "end": v(2.96, -43.43) * mm});
            skLineSegment(sketch, "E710", {"start": v(2.96, -43.43) * mm, "end": v(3.3, -42.93) * mm});
            skLineSegment(sketch, "E711", {"start": v(3.3, -42.93) * mm, "end": v(3.56, -42.33) * mm});
            skLineSegment(sketch, "E712", {"start": v(3.56, -42.33) * mm, "end": v(3.8, -41.83) * mm});
            skLineSegment(sketch, "E713", {"start": v(3.8, -41.83) * mm, "end": v(4.06, -41.32) * mm});
            skLineSegment(sketch, "E714", {"start": v(4.06, -41.32) * mm, "end": v(4.32, -40.8) * mm});
            skLineSegment(sketch, "E715", {"start": v(4.32, -40.8) * mm, "end": v(4.57, -40.22) * mm});
            skLineSegment(sketch, "E716", {"start": v(4.57, -40.22) * mm, "end": v(4.74, -39.7) * mm});
            skLineSegment(sketch, "E717", {"start": v(4.74, -39.7) * mm, "end": v(4.91, -39.2) * mm});
            skLineSegment(sketch, "E718", {"start": v(4.91, -39.2) * mm, "end": v(5.16, -38.7) * mm});
            skLineSegment(sketch, "E719", {"start": v(5.16, -38.7) * mm, "end": v(5.33, -38.1) * mm});
            skLineSegment(sketch, "E720", {"start": v(5.33, -38.1) * mm, "end": v(5.5, -37.6) * mm});
            skLineSegment(sketch, "E721", {"start": v(5.5, -37.6) * mm, "end": v(5.67, -37.08) * mm});
            skLineSegment(sketch, "E722", {"start": v(5.67, -37.08) * mm, "end": v(5.76, -36.58) * mm});
            skLineSegment(sketch, "E723", {"start": v(5.76, -36.58) * mm, "end": v(5.93, -35.98) * mm});
            skLineSegment(sketch, "E724", {"start": v(5.93, -35.98) * mm, "end": v(6.01, -35.48) * mm});
            skLineSegment(sketch, "E725", {"start": v(6.01, -35.48) * mm, "end": v(6.1, -34.97) * mm});
            skLineSegment(sketch, "E726", {"start": v(6.1, -34.97) * mm, "end": v(6.18, -34.46) * mm});
            skLineSegment(sketch, "E727", {"start": v(6.18, -34.46) * mm, "end": v(6.18, -33.95) * mm});
            skLineSegment(sketch, "E728", {"start": v(6.18, -33.95) * mm, "end": v(9.23, -33.53) * mm});
            skLineSegment(sketch, "E729", {"start": v(9.23, -33.53) * mm, "end": v(12.28, -33.02) * mm});
            skLineSegment(sketch, "E730", {"start": v(12.28, -33.02) * mm, "end": v(12.45, -33.44) * mm});
            skLineSegment(sketch, "E731", {"start": v(12.45, -33.44) * mm, "end": v(12.7, -33.95) * mm});
            skLineSegment(sketch, "E732", {"start": v(12.7, -33.95) * mm, "end": v(12.95, -34.37) * mm});
            skLineSegment(sketch, "E733", {"start": v(12.95, -34.37) * mm, "end": v(13.2, -34.88) * mm});
            skLineSegment(sketch, "E734", {"start": v(13.2, -34.88) * mm, "end": v(13.46, -35.3) * mm});
            skLineSegment(sketch, "E735", {"start": v(13.46, -35.3) * mm, "end": v(13.72, -35.81) * mm});
            skLineSegment(sketch, "E736", {"start": v(13.72, -35.81) * mm, "end": v(14.06, -36.24) * mm});
            skLineSegment(sketch, "E737", {"start": v(14.06, -36.24) * mm, "end": v(14.4, -36.66) * mm});
            skLineSegment(sketch, "E738", {"start": v(14.4, -36.66) * mm, "end": v(14.73, -37.17) * mm});
            skLineSegment(sketch, "E739", {"start": v(14.73, -37.17) * mm, "end": v(15.07, -37.6) * mm});
            skLineSegment(sketch, "E740", {"start": v(15.07, -37.6) * mm, "end": v(15.4, -38.02) * mm});
            skLineSegment(sketch, "E741", {"start": v(15.4, -38.02) * mm, "end": v(15.83, -38.44) * mm});
            skLineSegment(sketch, "E742", {"start": v(15.83, -38.44) * mm, "end": v(16.17, -38.86) * mm});
            skLineSegment(sketch, "E743", {"start": v(16.17, -38.86) * mm, "end": v(16.6, -39.29) * mm});
            skLineSegment(sketch, "E744", {"start": v(16.6, -39.29) * mm, "end": v(16.93, -39.7) * mm});
            skLineSegment(sketch, "E745", {"start": v(16.93, -39.7) * mm, "end": v(17.36, -40.13) * mm});
            skLineSegment(sketch, "E746", {"start": v(17.36, -40.13) * mm, "end": v(17.78, -40.55) * mm});
            skLineSegment(sketch, "E747", {"start": v(17.78, -40.55) * mm, "end": v(18.2, -40.98) * mm});
            skLineSegment(sketch, "E748", {"start": v(18.2, -40.98) * mm, "end": v(18.71, -41.4) * mm});
            skLineSegment(sketch, "E749", {"start": v(18.71, -41.4) * mm, "end": v(19.13, -41.83) * mm});
            skLineSegment(sketch, "E750", {"start": v(19.13, -41.83) * mm, "end": v(23.96, -40.22) * mm});
            skLineSegment(sketch, "E751", {"start": v(23.96, -40.22) * mm, "end": v(24.13, -39.62) * mm});
            skLineSegment(sketch, "E752", {"start": v(24.13, -39.62) * mm, "end": v(24.3, -39.03) * mm});
            skLineSegment(sketch, "E753", {"start": v(24.3, -39.03) * mm, "end": v(24.38, -38.44) * mm});
            skLineSegment(sketch, "E754", {"start": v(24.38, -38.44) * mm, "end": v(24.47, -37.85) * mm});
            skLineSegment(sketch, "E755", {"start": v(24.47, -37.85) * mm, "end": v(24.55, -37.25) * mm});
            skLineSegment(sketch, "E756", {"start": v(24.55, -37.25) * mm, "end": v(24.64, -36.74) * mm});
            skLineSegment(sketch, "E757", {"start": v(24.64, -36.74) * mm, "end": v(24.72, -36.15) * mm});
            skLineSegment(sketch, "E758", {"start": v(24.72, -36.15) * mm, "end": v(24.72, -35.56) * mm});
            skLineSegment(sketch, "E759", {"start": v(24.72, -35.56) * mm, "end": v(24.8, -34.97) * mm});
            skLineSegment(sketch, "E760", {"start": v(24.8, -34.97) * mm, "end": v(24.8, -34.46) * mm});
            skLineSegment(sketch, "E761", {"start": v(24.8, -34.46) * mm, "end": v(24.8, -33.87) * mm});
            skLineSegment(sketch, "E762", {"start": v(24.8, -33.87) * mm, "end": v(24.8, -33.27) * mm});
            skLineSegment(sketch, "E763", {"start": v(24.8, -33.27) * mm, "end": v(24.8, -32.77) * mm});
            skLineSegment(sketch, "E764", {"start": v(24.8, -32.77) * mm, "end": v(24.8, -32.17) * mm});
            skLineSegment(sketch, "E765", {"start": v(24.8, -32.17) * mm, "end": v(24.8, -31.67) * mm});
            skLineSegment(sketch, "E766", {"start": v(24.8, -31.67) * mm, "end": v(24.72, -31.16) * mm});
            skLineSegment(sketch, "E767", {"start": v(24.72, -31.16) * mm, "end": v(24.64, -30.56) * mm});
            skLineSegment(sketch, "E768", {"start": v(24.64, -30.56) * mm, "end": v(24.64, -30.06) * mm});
            skLineSegment(sketch, "E769", {"start": v(24.64, -30.06) * mm, "end": v(24.47, -29.55) * mm});
            skLineSegment(sketch, "E770", {"start": v(24.47, -29.55) * mm, "end": v(24.38, -29.04) * mm});
            skLineSegment(sketch, "E771", {"start": v(24.38, -29.04) * mm, "end": v(27.18, -27.69) * mm});
            skLineSegment(sketch, "E772", {"start": v(27.18, -27.69) * mm, "end": v(29.8, -26.25) * mm});
            skLineSegment(sketch, "E773", {"start": v(29.8, -26.25) * mm, "end": v(30.14, -26.67) * mm});
            skLineSegment(sketch, "E774", {"start": v(30.14, -26.67) * mm, "end": v(30.56, -27) * mm});
            skLineSegment(sketch, "E775", {"start": v(30.56, -27) * mm, "end": v(30.9, -27.43) * mm});
            skLineSegment(sketch, "E776", {"start": v(30.9, -27.43) * mm, "end": v(31.33, -27.77) * mm});
            skLineSegment(sketch, "E777", {"start": v(31.33, -27.77) * mm, "end": v(31.75, -28.1) * mm});
            skLineSegment(sketch, "E778", {"start": v(31.75, -28.1) * mm, "end": v(32.17, -28.45) * mm});
            skLineSegment(sketch, "E779", {"start": v(32.17, -28.45) * mm, "end": v(32.6, -28.79) * mm});
            skLineSegment(sketch, "E780", {"start": v(32.6, -28.79) * mm, "end": v(33.02, -29.13) * mm});
            skLineSegment(sketch, "E781", {"start": v(33.02, -29.13) * mm, "end": v(33.44, -29.46) * mm});
            skLineSegment(sketch, "E782", {"start": v(33.44, -29.46) * mm, "end": v(33.95, -29.8) * mm});
            skLineSegment(sketch, "E783", {"start": v(33.95, -29.8) * mm, "end": v(34.46, -30.06) * mm});
            skLineSegment(sketch, "E784", {"start": v(34.46, -30.06) * mm, "end": v(34.88, -30.4) * mm});
            skLineSegment(sketch, "E785", {"start": v(34.88, -30.4) * mm, "end": v(35.39, -30.65) * mm});
            skLineSegment(sketch, "E786", {"start": v(35.39, -30.65) * mm, "end": v(35.9, -30.99) * mm});
            skLineSegment(sketch, "E787", {"start": v(35.9, -30.99) * mm, "end": v(36.4, -31.24) * mm});
            skLineSegment(sketch, "E788", {"start": v(36.4, -31.24) * mm, "end": v(36.91, -31.5) * mm});
            skLineSegment(sketch, "E789", {"start": v(36.91, -31.5) * mm, "end": v(37.5, -31.75) * mm});
            skLineSegment(sketch, "E790", {"start": v(37.5, -31.75) * mm, "end": v(38.02, -32.09) * mm});
            skLineSegment(sketch, "E791", {"start": v(38.02, -32.09) * mm, "end": v(38.52, -32.26) * mm});
            skLineSegment(sketch, "E792", {"start": v(38.52, -32.26) * mm, "end": v(39.12, -32.51) * mm});
            skLineSegment(sketch, "E793", {"start": v(39.12, -32.51) * mm, "end": v(43.26, -29.55) * mm});
            skLineSegment(sketch, "E794", {"start": v(43.26, -29.55) * mm, "end": v(43.18, -28.96) * mm});
            skLineSegment(sketch, "E795", {"start": v(43.18, -28.96) * mm, "end": v(43.1, -28.36) * mm});
            skLineSegment(sketch, "E796", {"start": v(43.1, -28.36) * mm, "end": v(43.01, -27.69) * mm});
            skLineSegment(sketch, "E797", {"start": v(43.01, -27.69) * mm, "end": v(42.93, -27.18) * mm});
            skLineSegment(sketch, "E798", {"start": v(42.93, -27.18) * mm, "end": v(42.84, -26.59) * mm});
            skLineSegment(sketch, "E799", {"start": v(42.84, -26.59) * mm, "end": v(42.76, -26) * mm});
            skLineSegment(sketch, "E800", {"start": v(42.76, -26) * mm, "end": v(42.59, -25.4) * mm});
            skLineSegment(sketch, "E801", {"start": v(42.59, -25.4) * mm, "end": v(42.5, -24.9) * mm});
            skLineSegment(sketch, "E802", {"start": v(42.5, -24.9) * mm, "end": v(42.33, -24.3) * mm});
            skLineSegment(sketch, "E803", {"start": v(42.33, -24.3) * mm, "end": v(42.25, -23.7) * mm});
            skLineSegment(sketch, "E804", {"start": v(42.25, -23.7) * mm, "end": v(42.08, -23.2) * mm});
            skLineSegment(sketch, "E805", {"start": v(42.08, -23.2) * mm, "end": v(41.9, -22.69) * mm});
            skLineSegment(sketch, "E806", {"start": v(41.9, -22.69) * mm, "end": v(41.74, -22.18) * mm});
            skLineSegment(sketch, "E807", {"start": v(41.74, -22.18) * mm, "end": v(41.57, -21.67) * mm});
            skLineSegment(sketch, "E808", {"start": v(41.57, -21.67) * mm, "end": v(41.32, -21.08) * mm});
            skLineSegment(sketch, "E809", {"start": v(41.32, -21.08) * mm, "end": v(41.15, -20.66) * mm});
            skLineSegment(sketch, "E810", {"start": v(41.15, -20.66) * mm, "end": v(40.9, -20.15) * mm});
            skLineSegment(sketch, "E811", {"start": v(40.9, -20.15) * mm, "end": v(40.64, -19.64) * mm});
            skLineSegment(sketch, "E812", {"start": v(40.64, -19.64) * mm, "end": v(40.39, -19.22) * mm});
            skLineSegment(sketch, "E813", {"start": v(40.39, -19.22) * mm, "end": v(40.13, -18.71) * mm});
            skLineSegment(sketch, "E814", {"start": v(40.13, -18.71) * mm, "end": v(42.33, -16.68) * mm});
            skLineSegment(sketch, "E815", {"start": v(42.33, -16.68) * mm, "end": v(44.45, -14.48) * mm});
            skLineSegment(sketch, "E816", {"start": v(44.45, -14.48) * mm, "end": v(44.87, -14.73) * mm});
            skLineSegment(sketch, "E817", {"start": v(44.87, -14.73) * mm, "end": v(45.38, -14.99) * mm});
            skLineSegment(sketch, "E818", {"start": v(45.38, -14.99) * mm, "end": v(45.89, -15.15) * mm});
            skLineSegment(sketch, "E819", {"start": v(45.89, -15.15) * mm, "end": v(46.31, -15.4) * mm});
            skLineSegment(sketch, "E820", {"start": v(46.31, -15.4) * mm, "end": v(46.82, -15.58) * mm});
            skLineSegment(sketch, "E821", {"start": v(46.82, -15.58) * mm, "end": v(47.33, -15.83) * mm});
            skLineSegment(sketch, "E822", {"start": v(47.33, -15.83) * mm, "end": v(47.84, -16) * mm});
            skLineSegment(sketch, "E823", {"start": v(47.84, -16) * mm, "end": v(48.35, -16.17) * mm});
            skLineSegment(sketch, "E824", {"start": v(48.35, -16.17) * mm, "end": v(48.94, -16.34) * mm});
            skLineSegment(sketch, "E825", {"start": v(48.94, -16.34) * mm, "end": v(49.44, -16.5) * mm});
            skLineSegment(sketch, "E826", {"start": v(49.44, -16.5) * mm, "end": v(50.04, -16.68) * mm});
            skLineSegment(sketch, "E827", {"start": v(50.04, -16.68) * mm, "end": v(50.55, -16.76) * mm});
            skLineSegment(sketch, "E828", {"start": v(50.55, -16.76) * mm, "end": v(51.14, -16.93) * mm});
            skLineSegment(sketch, "E829", {"start": v(51.14, -16.93) * mm, "end": v(51.73, -17.02) * mm});
            skLineSegment(sketch, "E830", {"start": v(51.73, -17.02) * mm, "end": v(52.32, -17.1) * mm});
            skLineSegment(sketch, "E831", {"start": v(52.32, -17.1) * mm, "end": v(52.83, -17.27) * mm});
            skLineSegment(sketch, "E832", {"start": v(52.83, -17.27) * mm, "end": v(53.42, -17.36) * mm});
            skLineSegment(sketch, "E833", {"start": v(53.42, -17.36) * mm, "end": v(54.02, -17.36) * mm});
            skLineSegment(sketch, "E834", {"start": v(54.02, -17.36) * mm, "end": v(54.6, -17.44) * mm});
            skLineSegment(sketch, "E835", {"start": v(54.6, -17.44) * mm, "end": v(55.29, -17.53) * mm});
            skLineSegment(sketch, "E836", {"start": v(55.29, -17.53) * mm, "end": v(58.25, -13.38) * mm});
            skLineSegment(sketch, "E837", {"start": v(58.25, -13.38) * mm, "end": v(58, -12.87) * mm});
            skLineSegment(sketch, "E838", {"start": v(58, -12.87) * mm, "end": v(57.74, -12.28) * mm});
            skLineSegment(sketch, "E839", {"start": v(57.74, -12.28) * mm, "end": v(57.49, -11.77) * mm});
            skLineSegment(sketch, "E840", {"start": v(57.49, -11.77) * mm, "end": v(57.23, -11.18) * mm});
            skLineSegment(sketch, "E841", {"start": v(57.23, -11.18) * mm, "end": v(56.98, -10.67) * mm});
            skLineSegment(sketch, "E842", {"start": v(56.98, -10.67) * mm, "end": v(56.64, -10.16) * mm});
            skLineSegment(sketch, "E843", {"start": v(56.64, -10.16) * mm, "end": v(56.39, -9.65) * mm});
            skLineSegment(sketch, "E844", {"start": v(56.39, -9.65) * mm, "end": v(56.13, -9.14) * mm});
            skLineSegment(sketch, "E845", {"start": v(56.13, -9.14) * mm, "end": v(55.8, -8.72) * mm});
            skLineSegment(sketch, "E846", {"start": v(55.8, -8.72) * mm, "end": v(55.46, -8.21) * mm});
            skLineSegment(sketch, "E847", {"start": v(55.46, -8.21) * mm, "end": v(55.2, -7.79) * mm});
            skLineSegment(sketch, "E848", {"start": v(55.2, -7.79) * mm, "end": v(54.86, -7.28) * mm});
            skLineSegment(sketch, "E849", {"start": v(54.86, -7.28) * mm, "end": v(54.53, -6.86) * mm});
            skLineSegment(sketch, "E850", {"start": v(54.53, -6.86) * mm, "end": v(54.19, -6.43) * mm});
            skLineSegment(sketch, "E851", {"start": v(54.19, -6.43) * mm, "end": v(53.85, -6.01) * mm});
            skLineSegment(sketch, "E852", {"start": v(53.85, -6.01) * mm, "end": v(53.5, -5.59) * mm});
            skLineSegment(sketch, "E853", {"start": v(53.5, -5.59) * mm, "end": v(53.09, -5.16) * mm});
            skLineSegment(sketch, "E854", {"start": v(53.09, -5.16) * mm, "end": v(52.75, -4.83) * mm});
            skLineSegment(sketch, "E855", {"start": v(52.75, -4.83) * mm, "end": v(52.32, -4.49) * mm});
            skLineSegment(sketch, "E856", {"start": v(52.32, -4.49) * mm, "end": v(51.99, -4.06) * mm});
            skLineSegment(sketch, "E857", {"start": v(51.99, -4.06) * mm, "end": v(53.42, -1.44) * mm});
            skLineSegment(sketch, "E858", {"start": v(53.42, -1.44) * mm, "end": v(54.7, 1.36) * mm});
            skLineSegment(sketch, "E859", {"start": v(54.7, 1.36) * mm, "end": v(55.29, 1.19) * mm});
            skLineSegment(sketch, "E860", {"start": v(55.29, 1.19) * mm, "end": v(55.8, 1.1) * mm});
            skLineSegment(sketch, "E861", {"start": v(55.8, 1.1) * mm, "end": v(56.3, 1.02) * mm});
            skLineSegment(sketch, "E862", {"start": v(56.3, 1.02) * mm, "end": v(56.81, 1.02) * mm});
            skLineSegment(sketch, "E863", {"start": v(56.81, 1.02) * mm, "end": v(57.4, 0.93) * mm});
            skLineSegment(sketch, "E864", {"start": v(57.4, 0.93) * mm, "end": v(57.91, 0.93) * mm});
            skLineSegment(sketch, "E865", {"start": v(57.91, 0.93) * mm, "end": v(58.5, 0.85) * mm});
            skLineSegment(sketch, "E866", {"start": v(58.5, 0.85) * mm, "end": v(59.01, 0.85) * mm});
            skLineSegment(sketch, "E867", {"start": v(59.01, 0.85) * mm, "end": v(59.6, 0.85) * mm});
            skLineSegment(sketch, "E868", {"start": v(59.6, 0.85) * mm, "end": v(60.11, 0.93) * mm});
            skLineSegment(sketch, "E869", {"start": v(60.11, 0.93) * mm, "end": v(60.7, 0.93) * mm});
            skLineSegment(sketch, "E870", {"start": v(60.7, 0.93) * mm, "end": v(61.3, 1.02) * mm});
            skLineSegment(sketch, "E871", {"start": v(61.3, 1.02) * mm, "end": v(61.8, 1.02) * mm});
            skLineSegment(sketch, "E872", {"start": v(61.8, 1.02) * mm, "end": v(62.4, 1.1) * mm});
            skLineSegment(sketch, "E873", {"start": v(62.4, 1.1) * mm, "end": v(63, 1.19) * mm});
            skLineSegment(sketch, "E874", {"start": v(63, 1.19) * mm, "end": v(63.58, 1.27) * mm});
            skLineSegment(sketch, "E875", {"start": v(63.58, 1.27) * mm, "end": v(64.18, 1.36) * mm});
            skLineSegment(sketch, "E876", {"start": v(64.18, 1.36) * mm, "end": v(64.77, 1.44) * mm});
            skLineSegment(sketch, "E877", {"start": v(64.77, 1.44) * mm, "end": v(65.36, 1.6) * mm});
            skLineSegment(sketch, "E878", {"start": v(65.36, 1.6) * mm, "end": v(65.95, 1.7) * mm});
            skLineSegment(sketch, "E879", {"start": v(65.95, 1.7) * mm, "end": v(67.56, 6.6) * mm});
            skLineSegment(sketch, "E880", {"start": v(67.56, 6.6) * mm, "end": v(67.14, 7.03) * mm});
            skLineSegment(sketch, "E881", {"start": v(67.14, 7.03) * mm, "end": v(66.72, 7.45) * mm});
            skLineSegment(sketch, "E882", {"start": v(66.72, 7.45) * mm, "end": v(66.3, 7.87) * mm});
            skLineSegment(sketch, "E883", {"start": v(66.3, 7.87) * mm, "end": v(65.87, 8.3) * mm});
            skLineSegment(sketch, "E884", {"start": v(65.87, 8.3) * mm, "end": v(65.45, 8.72) * mm});
            skLineSegment(sketch, "E885", {"start": v(65.45, 8.72) * mm, "end": v(65.02, 9.14) * mm});
            skLineSegment(sketch, "E886", {"start": v(65.02, 9.14) * mm, "end": v(64.6, 9.57) * mm});
            skLineSegment(sketch, "E887", {"start": v(64.6, 9.57) * mm, "end": v(64.18, 9.9) * mm});
            skLineSegment(sketch, "E888", {"start": v(64.18, 9.9) * mm, "end": v(63.75, 10.25) * mm});
            skLineSegment(sketch, "E889", {"start": v(63.75, 10.25) * mm, "end": v(63.33, 10.67) * mm});
            skLineSegment(sketch, "E890", {"start": v(63.33, 10.67) * mm, "end": v(62.82, 11) * mm});
            skLineSegment(sketch, "E891", {"start": v(62.82, 11) * mm, "end": v(62.4, 11.34) * mm});
            skLineSegment(sketch, "E892", {"start": v(62.4, 11.34) * mm, "end": v(61.98, 11.68) * mm});
            skLineSegment(sketch, "E893", {"start": v(61.98, 11.68) * mm, "end": v(61.47, 11.94) * mm});
            skLineSegment(sketch, "E894", {"start": v(61.47, 11.94) * mm, "end": v(61.05, 12.28) * mm});
            skLineSegment(sketch, "E895", {"start": v(61.05, 12.28) * mm, "end": v(60.62, 12.53) * mm});
            skLineSegment(sketch, "E896", {"start": v(60.62, 12.53) * mm, "end": v(60.11, 12.78) * mm});
            skLineSegment(sketch, "E897", {"start": v(60.11, 12.78) * mm, "end": v(59.6, 13.04) * mm});
            skLineSegment(sketch, "E898", {"start": v(59.6, 13.04) * mm, "end": v(59.18, 13.3) * mm});
            skLineSegment(sketch, "E899", {"start": v(59.18, 13.3) * mm, "end": v(58.67, 13.46) * mm});
            skLineSegment(sketch, "E900", {"start": v(58.67, 13.46) * mm, "end": v(59.27, 16.5) * mm});
            skSolve(sketch);
        }
        {
            var Q0;
            Q0=makeQuery(id+"F0.imprint","IMPRINT",FACE,{"disambiguationData":[TD([[makeQuery(id+"F0.imprint","IMPRINT",EDGE,{"derivedFrom":sQuery(id+"F0.wireOp",EDGE,"E1")}),1.0]])]});
            extrude(context, id + "F1", {"entities" : qUnion([Q0]), "depth" : 25.4 * mm});
        }
    });
